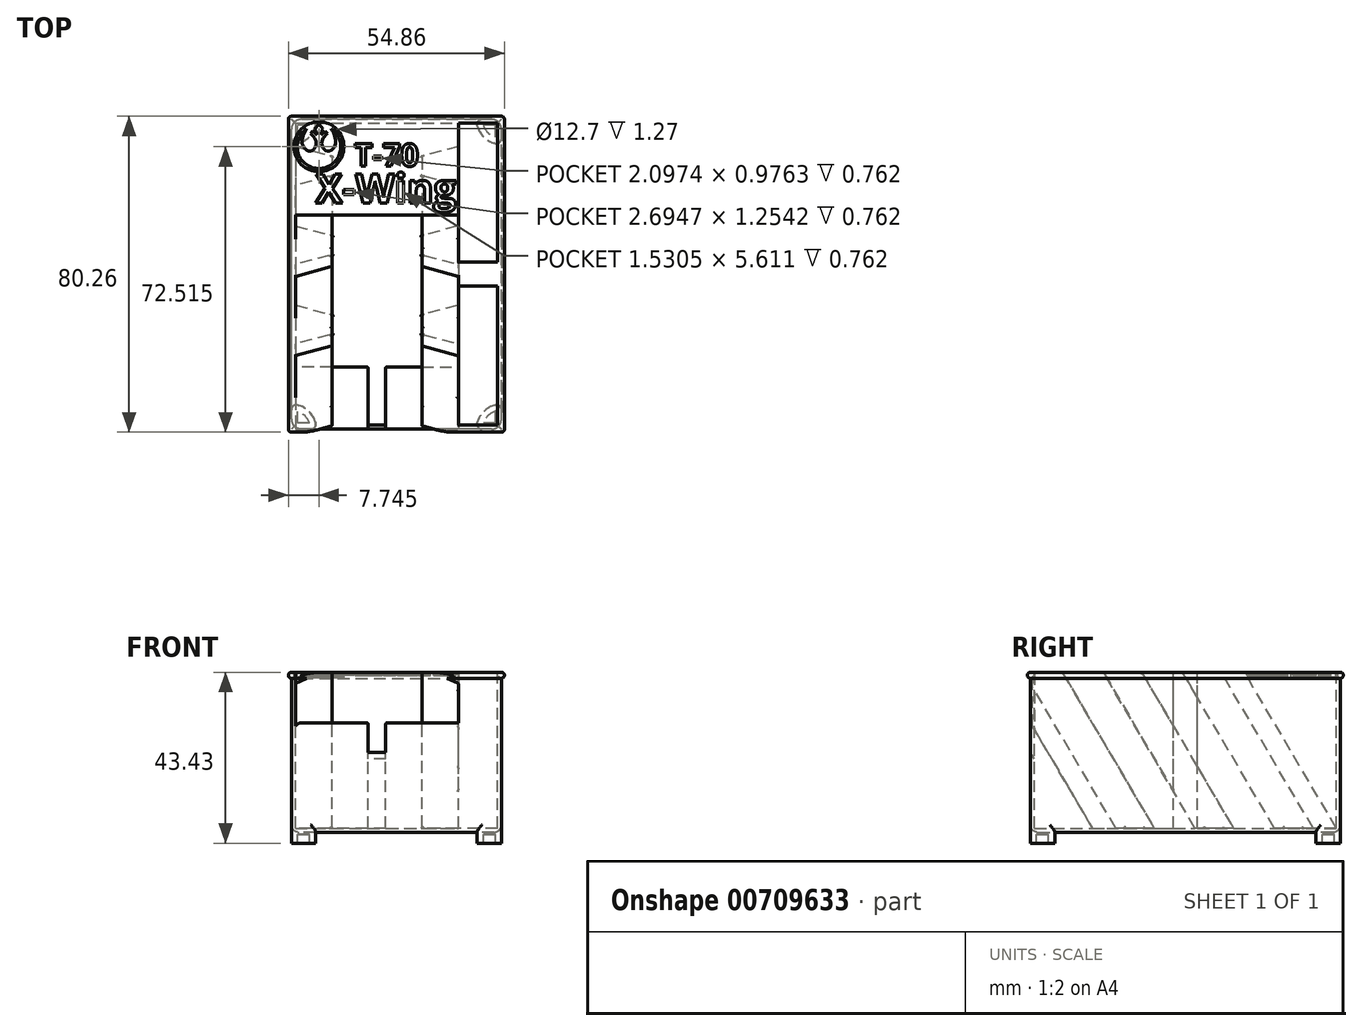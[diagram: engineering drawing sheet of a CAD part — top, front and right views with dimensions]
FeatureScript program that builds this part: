
annotation { "Feature Type Name" : "Feature", "Feature Type Description" : "" }
export const myFeature = defineFeature(function(context is Context, id is Id, definition is map)
    precondition{}
    {
        {
            var Q0;
            Q0=qCreatedBy(makeId("Top.planeOp"),FACE);
            var sketch = newSketch(context, id + "F0", { "sketchPlane" : qUnion([Q0])});
            skLineSegment(sketch, "E0.bottom", {"start": v(25.15, 37.85) * mm, "end": v(-25.15, 37.85) * mm});
            skLineSegment(sketch, "E0.top", {"start": v(25.15, -37.85) * mm, "end": v(-25.15, -37.85) * mm});
            skLineSegment(sketch, "E0.left", {"start": v(25.15, 37.85) * mm, "end": v(25.15, -37.85) * mm});
            skLineSegment(sketch, "E0.right", {"start": v(-25.15, 37.85) * mm, "end": v(-25.15, -37.85) * mm});
            skPoint(sketch, "E0.middle", {"position": v(0, 0) * mm});
            skSolve(sketch);
        }
        {
            var Q0;
            Q0=qCreatedBy(makeId("Front.planeOp"),FACE);
            var sketch = newSketch(context, id + "F1", { "sketchPlane" : qUnion([Q0])});
            skLineSegment(sketch, "E1.bottom", {"start": v(26.67, -20.32) * mm, "end": v(-26.67, -20.32) * mm});
            skLineSegment(sketch, "E1.top", {"start": v(26.67, 20.32) * mm, "end": v(-26.67, 20.32) * mm});
            skLineSegment(sketch, "E1.left", {"start": v(26.67, -20.32) * mm, "end": v(26.67, 20.32) * mm});
            skLineSegment(sketch, "E1.right", {"start": v(-26.67, -20.32) * mm, "end": v(-26.67, 20.32) * mm});
            skPoint(sketch, "E1.middle", {"position": v(0, 0) * mm});
            skSolve(sketch);
        }
        {
            var Q0;
            Q0=qSketchRegion(id+"F1",true);
            extrude(context, id + "F2", {"entities" : qUnion([Q0]), "depth" : 78.74 * mm, "offsetDistance" : 25.4 * mm, "symmetric" : true});
        }
        {
            var Q0;
            Q0=makeQuery(id+"F2.opExtrude","SWEPT_FACE",FACE,{"disambiguationData":[OSD([sQuery(id+"F1.wireOp",EDGE,"E1.top")])]});
            shell(context, id + "F3", {"entities" : qUnion([Q0]), "thickness" : 1.02 * mm});
        }
        {
            var Q0;
            {var subQ0=sQuery(id+"F1.wireOp",EDGE,"E1.right");var subQ3=sQuery(id+"F1.wireOp",EDGE,"E1.top");Q0=makeQuery(id+"F16.boolean.opBoolean","SPLIT",EDGE,{"disambiguationData":[TD([makeQuery(id+"F3.opShell","OFFSET_FACE",FACE,{"disambiguationData":[OSD([subQ0])]})])],"derivedFrom":makeQuery(id+"F3.opShell","OFFSET_EDGE",EDGE,{"disambiguationData":[OSD([subQ3]),TDD([makeQuery(id+"F2.opExtrude","CAP_EDGE",EDGE,{"disambiguationData":[OSD([subQ3])],"isStart":false})])]})});}
            var Q1;
            {var subQ0=sQuery(id+"F7.wireOp",EDGE,"E9");var subQ1=sQuery(id+"F1.wireOp",EDGE,"E1.right");var subQ2=sQuery(id+"F1.wireOp",EDGE,"E1.top");var subQ3=makeQuery(id+"F2.opExtrude","CAP_EDGE",EDGE,{"disambiguationData":[OSD([subQ2])],"isStart":false});Q1=makeQuery(id+"F8.boolean.opBoolean","MERGE",EDGE,{"derivedFrom":[subQ3,makeQuery(id+"F8.opSweep","SWEPT_EDGE",EDGE,{"disambiguationData":[OSD([subQ2,subQ1,subQ0]),TDD([subQ3,makeQuery(id+"F7.imprint","INTERSECT",VERTEX,{"derivedFrom":[subQ3,makeQuery(id+"F2.opExtrude","CAP_EDGE",EDGE,{"disambiguationData":[OSD([subQ1])],"isStart":false}),subQ0]})])]})]});}
            cPlane(context, id + "F4", {"entities" : qUnion([Q0, Q1]), "cplaneType" : CPlaneType.LINE_ANGLE, "offset" : 25.4 * mm, "angle" : 30.5 * degree, "oppositeDirection" : true, "width" : 152.4 * mm, "height" : 152.4 * mm});
        }
        {
            var Q0;
            Q0=makeQuery(id+"F3.opShell","OFFSET_FACE",FACE,{"disambiguationData":[OSD([sQuery(id+"F1.wireOp",EDGE,"E1.right")])]});
            var sketch = newSketch(context, id + "F5", { "sketchPlane" : qUnion([Q0])});
            skLineSegment(sketch, "E2.0", {"start": v(38.35, -19.3) * mm, "end": v(38.35, 20.32) * mm});
            skLineSegment(sketch, "E3.1", {"start": v(-38.35, -19.3) * mm, "end": v(38.35, -19.3) * mm});
            skLineSegment(sketch, "E4", {"start": v(38.35, -19.3) * mm, "end": v(-5.55, 55.23) * mm});
            skLineSegment(sketch, "E5.0", {"start": v(-38.35, 20.32) * mm, "end": v(38.35, 20.32) * mm});
            skPoint(sketch, "E6", {"position": v(15.01, 20.32) * mm});
            skSolve(sketch);
        }
        {
            var Q0;
            Q0=qCreatedBy(id+"F4.planeOp",FACE);
            var sketch = newSketch(context, id + "F6", { "sketchPlane" : qUnion([Q0])});
            skPoint(sketch, "E7.0", {"position": v(-25.65, 23.25) * mm});
            skSolve(sketch);
        }
        {
            var Q0;
            Q0=makeQuery(id+"F2.opExtrude","CAP_FACE",FACE,{"disambiguationData":[OSD([sQuery(id+"F1.wireOp",EDGE,"E1.bottom"),sQuery(id+"F1.wireOp",EDGE,"E1.top"),sQuery(id+"F1.wireOp",EDGE,"E1.left"),sQuery(id+"F1.wireOp",EDGE,"E1.right")])],"isStart":false});
            var sketch = newSketch(context, id + "F7", { "sketchPlane" : qUnion([Q0])});
            skArc(sketch, "E8", {"start": v(-122.9, 118.26) * mm, "mid": v(-123.67, 117.5) * mm, "end": v(-122.9, 116.74) * mm});
            skArc(sketch, "E9", {"start": v(-26.67, 20.32) * mm, "mid": v(-27.43, 19.56) * mm, "end": v(-26.67, 18.8) * mm});
            skSolve(sketch);
        }
        {
            var Q0;
            {var subQ0=sQuery(id+"F7.wireOp",EDGE,"E9");Q0=makeQuery(id+"F7.imprint","IMPRINT",FACE,{"disambiguationData":[TD([[makeQuery(id+"F7.imprint","IMPRINT",EDGE,{"derivedFrom":subQ0}),1.0]])]});}
            var Q1;
            Q1=makeQuery(id+"F2.opExtrude","CAP_EDGE",EDGE,{"disambiguationData":[OSD([sQuery(id+"F1.wireOp",EDGE,"E1.top")])],"isStart":false});
            var Q2;
            Q2=makeQuery(id+"F2.opExtrude","SWEPT_EDGE",EDGE,{"disambiguationData":[OSD([sQuery(id+"F1.wireOp",EDGE,"E1.top"),sQuery(id+"F1.wireOp",EDGE,"E1.right")])]});
            var Q3;
            Q3=makeQuery(id+"F2.opExtrude","SWEPT_EDGE",EDGE,{"disambiguationData":[OSD([sQuery(id+"F1.wireOp",EDGE,"E1.top"),sQuery(id+"F1.wireOp",EDGE,"E1.left")])]});
            var Q4;
            Q4=makeQuery(id+"F2.opExtrude","CAP_EDGE",EDGE,{"disambiguationData":[OSD([sQuery(id+"F1.wireOp",EDGE,"E1.top")])],"isStart":true});
            sweep(context, id + "F8", {"operationType" : NewBodyOperationType.ADD, "profiles" : qUnion([Q0]), "path" : qUnion([Q1, Q2, Q3, Q4])});
        }
        {
            var Q0;
            Q0=makeQuery(id+"F2.opExtrude","SWEPT_FACE",FACE,{"disambiguationData":[OSD([sQuery(id+"F1.wireOp",EDGE,"E1.bottom")])]});
            var sketch = newSketch(context, id + "F9", { "sketchPlane" : qUnion([Q0])});
            skLineSegment(sketch, "E10.bottom", {"start": v(26.67, 39.37) * mm, "end": v(21.75, 39.37) * mm});
            skLineSegment(sketch, "E10.left", {"start": v(26.67, 39.37) * mm, "end": v(26.67, 34.45) * mm});
            skPoint(sketch, "E11.newPointA", {"position": v(20.32, 19.05) * mm});
            skArc(sketch, "E12", {"start": v(20.52, 37.78) * mm, "mid": v(22.18, 34.88) * mm, "end": v(25.08, 33.22) * mm});
            skPoint(sketch, "E13.visualSharp", {"position": v(20.32, 39.37) * mm});
            skArc(sketch, "E13.filletArc", {"start": v(21.75, 39.37) * mm, "mid": v(20.75, 38.88) * mm, "end": v(20.52, 37.78) * mm});
            skPoint(sketch, "E14.visualSharp", {"position": v(26.67, 33.02) * mm});
            skArc(sketch, "E14.filletArc", {"start": v(25.08, 33.22) * mm, "mid": v(26.18, 33.45) * mm, "end": v(26.67, 34.45) * mm});
            skArc(sketch, "E15.MirrorCS", {"start": v(-21.75, 39.37) * mm, "mid": v(-20.75, 38.88) * mm, "end": v(-20.52, 37.78) * mm});
            skArc(sketch, "E16.MirrorCS", {"start": v(-20.52, 37.78) * mm, "mid": v(-22.18, 34.88) * mm, "end": v(-25.08, 33.22) * mm});
            skArc(sketch, "E17.MirrorCS", {"start": v(-25.08, 33.22) * mm, "mid": v(-26.18, 33.45) * mm, "end": v(-26.67, 34.45) * mm});
            skLineSegment(sketch, "E18.MirrorCS", {"start": v(-26.67, 39.37) * mm, "end": v(-26.67, 34.45) * mm});
            skLineSegment(sketch, "E19.MirrorCS", {"start": v(-26.67, 39.37) * mm, "end": v(-21.75, 39.37) * mm});
            skArc(sketch, "E20.MirrorCS", {"start": v(-20.52, -37.78) * mm, "mid": v(-22.18, -34.88) * mm, "end": v(-25.08, -33.22) * mm});
            skArc(sketch, "E21.MirrorCS", {"start": v(-21.75, -39.37) * mm, "mid": v(-20.75, -38.88) * mm, "end": v(-20.52, -37.78) * mm});
            skLineSegment(sketch, "E22.MirrorCS", {"start": v(-26.67, -39.37) * mm, "end": v(-21.75, -39.37) * mm});
            skLineSegment(sketch, "E23.MirrorCS", {"start": v(-26.67, -39.37) * mm, "end": v(-26.67, -34.45) * mm});
            skArc(sketch, "E24.MirrorCS", {"start": v(-25.08, -33.22) * mm, "mid": v(-26.18, -33.45) * mm, "end": v(-26.67, -34.45) * mm});
            skArc(sketch, "E25.MirrorCS", {"start": v(21.75, -39.37) * mm, "mid": v(20.75, -38.88) * mm, "end": v(20.52, -37.78) * mm});
            skArc(sketch, "E26.MirrorCS", {"start": v(20.52, -37.78) * mm, "mid": v(22.18, -34.88) * mm, "end": v(25.08, -33.22) * mm});
            skArc(sketch, "E27.MirrorCS", {"start": v(25.08, -33.22) * mm, "mid": v(26.18, -33.45) * mm, "end": v(26.67, -34.45) * mm});
            skLineSegment(sketch, "E28.MirrorCS", {"start": v(26.67, -39.37) * mm, "end": v(26.67, -34.45) * mm});
            skLineSegment(sketch, "E29.MirrorCS", {"start": v(26.67, -39.37) * mm, "end": v(21.75, -39.37) * mm});
            skSolve(sketch);
        }
        {
            var Q0;
            Q0=qSketchRegion(id+"F9",true);
            extrude(context, id + "F10", {"entities" : qUnion([Q0]), "operationType" : NewBodyOperationType.ADD, "depth" : 2.8 * mm, "offsetDistance" : 25.4 * mm});
        }
        {
            var Q0;
            Q0=makeQuery(id+"F10.opExtrude","CAP_FACE",FACE,{"disambiguationData":[OSD([sQuery(id+"F9.wireOp",EDGE,"E16.MirrorCS"),sQuery(id+"F9.wireOp",EDGE,"E17.MirrorCS"),sQuery(id+"F9.wireOp",EDGE,"E18.MirrorCS"),sQuery(id+"F9.wireOp",EDGE,"E15.MirrorCS"),sQuery(id+"F9.wireOp",EDGE,"E19.MirrorCS")])],"isStart":false});
            var Q1;
            Q1=makeQuery(id+"F10.opExtrude","CAP_FACE",FACE,{"disambiguationData":[OSD([sQuery(id+"F9.wireOp",EDGE,"E10.bottom"),sQuery(id+"F9.wireOp",EDGE,"E10.left"),sQuery(id+"F9.wireOp",EDGE,"E12"),sQuery(id+"F9.wireOp",EDGE,"E13.filletArc"),sQuery(id+"F9.wireOp",EDGE,"E14.filletArc")])],"isStart":false});
            var Q2;
            Q2=makeQuery(id+"F10.opExtrude","CAP_FACE",FACE,{"disambiguationData":[OSD([sQuery(id+"F9.wireOp",EDGE,"E25.MirrorCS"),sQuery(id+"F9.wireOp",EDGE,"E26.MirrorCS"),sQuery(id+"F9.wireOp",EDGE,"E27.MirrorCS"),sQuery(id+"F9.wireOp",EDGE,"E28.MirrorCS"),sQuery(id+"F9.wireOp",EDGE,"E29.MirrorCS")])],"isStart":false});
            var Q3;
            Q3=makeQuery(id+"F10.opExtrude","CAP_FACE",FACE,{"disambiguationData":[OSD([sQuery(id+"F9.wireOp",EDGE,"E20.MirrorCS"),sQuery(id+"F9.wireOp",EDGE,"E21.MirrorCS"),sQuery(id+"F9.wireOp",EDGE,"E22.MirrorCS"),sQuery(id+"F9.wireOp",EDGE,"E23.MirrorCS"),sQuery(id+"F9.wireOp",EDGE,"E24.MirrorCS")])],"isStart":false});
            shell(context, id + "F11", {"entities" : qUnion([Q0, Q1, Q2, Q3]), "thickness" : 1.52 * mm});
        }
        {
            var Q0;
            Q0=makeQuery(id+"F8.opSweep","MID_CAP_EDGE",EDGE,{"disambiguationData":[OSD([sQuery(id+"F1.wireOp",EDGE,"E1.top"),sQuery(id+"F1.wireOp",EDGE,"E1.right"),sQuery(id+"F7.wireOp",EDGE,"E9")])],"capPos":1.0});
            var Q1;
            Q1=makeQuery(id+"F8.opSweep","CAP_EDGE",EDGE,{"disambiguationData":[OSD([sQuery(id+"F1.wireOp",EDGE,"E1.top"),sQuery(id+"F1.wireOp",EDGE,"E1.right"),sQuery(id+"F7.wireOp",EDGE,"E9")])],"isStart":true});
            var Q2;
            Q2=makeQuery(id+"F8.opSweep","MID_CAP_EDGE",EDGE,{"disambiguationData":[OSD([sQuery(id+"F1.wireOp",EDGE,"E1.top"),sQuery(id+"F1.wireOp",EDGE,"E1.left"),sQuery(id+"F7.wireOp",EDGE,"E9")])],"capPos":3.0});
            var Q3;
            Q3=makeQuery(id+"F8.opSweep","MID_CAP_EDGE",EDGE,{"disambiguationData":[OSD([sQuery(id+"F1.wireOp",EDGE,"E1.top"),sQuery(id+"F1.wireOp",EDGE,"E1.left"),sQuery(id+"F7.wireOp",EDGE,"E9")])],"capPos":2.0});
            fillet(context, id + "F12", {"entities" : qUnion([Q0, Q1, Q2, Q3]), "radius" : 0.76 * mm, "tangentPropagation" : true, "allowEdgeOverflow" : false});
        }
        {
            var Q0;
            Q0=makeQuery(id+"F10.boolean.opBoolean","MERGE",EDGE,{"derivedFrom":[makeQuery(id+"F2.opExtrude","CAP_EDGE",EDGE,{"disambiguationData":[OSD([sQuery(id+"F1.wireOp",EDGE,"E1.right")])],"isStart":false}),makeQuery(id+"F10.opExtrude","SWEPT_EDGE",EDGE,{"disambiguationData":[OSD([sQuery(id+"F9.wireOp",EDGE,"E18.MirrorCS"),sQuery(id+"F9.wireOp",EDGE,"E19.MirrorCS")])]})]});
            var Q1;
            Q1=makeQuery(id+"F10.boolean.opBoolean","MERGE",EDGE,{"derivedFrom":[makeQuery(id+"F2.opExtrude","CAP_EDGE",EDGE,{"disambiguationData":[OSD([sQuery(id+"F1.wireOp",EDGE,"E1.left")])],"isStart":false}),makeQuery(id+"F10.opExtrude","SWEPT_EDGE",EDGE,{"disambiguationData":[OSD([sQuery(id+"F9.wireOp",EDGE,"E10.bottom"),sQuery(id+"F9.wireOp",EDGE,"E10.left")])]})]});
            var Q2;
            Q2=makeQuery(id+"F10.boolean.opBoolean","MERGE",EDGE,{"derivedFrom":[makeQuery(id+"F2.opExtrude","CAP_EDGE",EDGE,{"disambiguationData":[OSD([sQuery(id+"F1.wireOp",EDGE,"E1.left")])],"isStart":true}),makeQuery(id+"F10.opExtrude","SWEPT_EDGE",EDGE,{"disambiguationData":[OSD([sQuery(id+"F9.wireOp",EDGE,"E28.MirrorCS"),sQuery(id+"F9.wireOp",EDGE,"E29.MirrorCS")])]})]});
            var Q3;
            Q3=makeQuery(id+"F10.boolean.opBoolean","MERGE",EDGE,{"derivedFrom":[makeQuery(id+"F2.opExtrude","CAP_EDGE",EDGE,{"disambiguationData":[OSD([sQuery(id+"F1.wireOp",EDGE,"E1.right")])],"isStart":true}),makeQuery(id+"F10.opExtrude","SWEPT_EDGE",EDGE,{"disambiguationData":[OSD([sQuery(id+"F9.wireOp",EDGE,"E22.MirrorCS"),sQuery(id+"F9.wireOp",EDGE,"E23.MirrorCS")])]})]});
            fillet(context, id + "F13", {"entities" : qUnion([Q0, Q1, Q2, Q3]), "radius" : 2.54 * mm, "tangentPropagation" : true, "allowEdgeOverflow" : false});
        }
        {
            var Q0;
            Q0=makeQuery(id+"F2.opExtrude","SWEPT_EDGE",EDGE,{"disambiguationData":[OSD([sQuery(id+"F1.wireOp",EDGE,"E1.bottom"),sQuery(id+"F1.wireOp",EDGE,"E1.right")])]});
            var Q1;
            Q1=makeQuery(id+"F2.opExtrude","CAP_EDGE",EDGE,{"disambiguationData":[OSD([sQuery(id+"F1.wireOp",EDGE,"E1.bottom")])],"isStart":false});
            var Q2;
            Q2=makeQuery(id+"F2.opExtrude","SWEPT_EDGE",EDGE,{"disambiguationData":[OSD([sQuery(id+"F1.wireOp",EDGE,"E1.bottom"),sQuery(id+"F1.wireOp",EDGE,"E1.left")])]});
            var Q3;
            Q3=makeQuery(id+"F2.opExtrude","CAP_EDGE",EDGE,{"disambiguationData":[OSD([sQuery(id+"F1.wireOp",EDGE,"E1.bottom")])],"isStart":true});
            fillet(context, id + "F14", {"entities" : qUnion([Q0, Q1, Q2, Q3]), "radius" : 1.9 * mm, "tangentPropagation" : true, "allowEdgeOverflow" : false});
        }
        {
            var Q0;
            Q0=makeQuery(id+"F24.boolean.opBoolean","MERGE",FACE,{"derivedFrom":[makeQuery(id+"F2.opExtrude","SWEPT_FACE",FACE,{"disambiguationData":[OSD([sQuery(id+"F1.wireOp",EDGE,"E1.top")])]}),makeQuery(id+"F24.opExtrude","CAP_FACE",FACE,{"disambiguationData":[OSD([sQuery(id+"F23.wireOp",EDGE,"CeT5EqMD-vzeh-J7pB-LkoM-5uFaC58c3kCY.bottom"),sQuery(id+"F23.wireOp",EDGE,"CeT5EqMD-vzeh-J7pB-LkoM-5uFaC58c3kCY.top"),sQuery(id+"F23.wireOp",EDGE,"CeT5EqMD-vzeh-J7pB-LkoM-5uFaC58c3kCY.left"),sQuery(id+"F23.wireOp",EDGE,"CeT5EqMD-vzeh-J7pB-LkoM-5uFaC58c3kCY.right")])],"isStart":true})]});
            var sketch = newSketch(context, id + "F15", { "sketchPlane" : qUnion([Q0])});
            skLineSegment(sketch, "E30.bottom", {"start": v(25.65, 38.35) * mm, "end": v(15.75, 38.35) * mm});
            skLineSegment(sketch, "E30.top", {"start": v(25.65, 3.05) * mm, "end": v(15.75, 3.05) * mm});
            skLineSegment(sketch, "E30.left", {"start": v(25.65, 38.35) * mm, "end": v(25.65, 3.05) * mm});
            skLineSegment(sketch, "E30.right", {"start": v(15.75, 38.35) * mm, "end": v(15.75, 3.05) * mm});
            skLineSegment(sketch, "E31.bottom", {"start": v(25.65, -38.35) * mm, "end": v(15.75, -38.35) * mm});
            skLineSegment(sketch, "E31.top", {"start": v(25.65, -3.05) * mm, "end": v(15.75, -3.05) * mm});
            skLineSegment(sketch, "E31.left", {"start": v(25.65, -38.35) * mm, "end": v(25.65, -3.05) * mm});
            skLineSegment(sketch, "E31.right", {"start": v(15.75, -38.35) * mm, "end": v(15.75, -3.05) * mm});
            skLineSegment(sketch, "E32.bottom", {"start": v(25.65, 38.35) * mm, "end": v(-25.65, 38.35) * mm});
            skLineSegment(sketch, "E32.top", {"start": v(25.65, -38.35) * mm, "end": v(-25.65, -38.35) * mm});
            skLineSegment(sketch, "E32.left", {"start": v(25.65, 38.35) * mm, "end": v(25.65, -38.35) * mm});
            skLineSegment(sketch, "E32.right", {"start": v(-25.65, 38.35) * mm, "end": v(-25.65, -38.35) * mm});
            skLineSegment(sketch, "E33", {"start": v(15.75, -38.35) * mm, "end": v(15.75, -38.35) * mm});
            skLineSegment(sketch, "E34", {"start": v(15.75, -38.35) * mm, "end": v(15.75, 38.35) * mm});
            skLineSegment(sketch, "E35.0", {"start": v(-25.65, 38.35) * mm, "end": v(-25.65, -5.55) * mm});
            skPoint(sketch, "E36.0", {"position": v(-25.65, 15.01) * mm});
            skLineSegment(sketch, "E37", {"start": v(-25.65, 15.01) * mm, "end": v(15.75, 15.01) * mm});
            skSolve(sketch);
        }
        {
            var Q0;
            {var subQ3=sQuery(id+"F15.wireOp",EDGE,"E30.top");Q0=makeQuery(id+"F15.imprint","IMPRINT",FACE,{"disambiguationData":[TD([[makeQuery(id+"F15.imprint","IMPRINT",EDGE,{"derivedFrom":subQ3}),1.0]])]});}
            var Q1;
            {var subQ5=sQuery(id+"F15.wireOp",EDGE,"E37");Q1=makeQuery(id+"F15.imprint","IMPRINT",FACE,{"disambiguationData":[TD([[makeQuery(id+"F15.imprint","IMPRINT",EDGE,{"derivedFrom":subQ5}),1.0]])]});}
            var Q2;
            Q2=makeQuery(id+"F3.opShell","OFFSET_FACE",FACE,{"disambiguationData":[OSD([sQuery(id+"F1.wireOp",EDGE,"E1.bottom")])]});
            extrude(context, id + "F16", {"entities" : qUnion([Q0, Q1]), "operationType" : NewBodyOperationType.ADD, "endBound" : BoundingType.UP_TO_SURFACE, "oppositeDirection" : true, "depth" : 25.4 * mm, "endBoundEntityFace" : qUnion([Q2]), "offsetDistance" : 25.4 * mm});
        }
        {
            var Q0;
            Q0=qCreatedBy(id+"F4.planeOp",FACE);
            var sketch = newSketch(context, id + "F17", { "sketchPlane" : qUnion([Q0])});
            skLineSegment(sketch, "E38.0", {"start": v(-25.65, -16.56) * mm, "end": v(-25.65, -7.67) * mm});
            skLineSegment(sketch, "E39", {"start": v(-25.65, 23.25) * mm, "end": v(-4.95, 23.25) * mm});
            skPoint(sketch, "E40.0", {"position": v(-25.65, 23.25) * mm});
            skLineSegment(sketch, "E41", {"start": v(-25.65, 23.25) * mm, "end": v(-25.65, 18.17) * mm});
            skLineSegment(sketch, "E42", {"start": v(-25.65, 18.17) * mm, "end": v(-16.37, 16.03) * mm});
            skLineSegment(sketch, "E43", {"start": v(-16.37, 16.03) * mm, "end": v(-16.37, 11.84) * mm});
            skLineSegment(sketch, "E44", {"start": v(-16.37, 11.84) * mm, "end": v(-25.65, 9.7) * mm});
            skLineSegment(sketch, "E45", {"start": v(-25.65, 9.7) * mm, "end": v(-25.65, 0.8) * mm});
            skLineSegment(sketch, "E46", {"start": v(-25.65, 0.8) * mm, "end": v(-16.37, -1.34) * mm});
            skLineSegment(sketch, "E47", {"start": v(-16.37, -1.34) * mm, "end": v(-16.37, -5.53) * mm});
            skLineSegment(sketch, "E48", {"start": v(-16.37, -5.53) * mm, "end": v(-25.65, -7.67) * mm});
            skLineSegment(sketch, "E49", {"start": v(-25.65, -7.67) * mm, "end": v(-25.65, -16.56) * mm});
            skLineSegment(sketch, "E50", {"start": v(-25.65, -16.56) * mm, "end": v(-16.37, -18.7) * mm});
            skLineSegment(sketch, "E51", {"start": v(-16.37, -18.7) * mm, "end": v(-16.37, -22.9) * mm});
            skLineSegment(sketch, "E52", {"start": v(-16.37, -22.9) * mm, "end": v(-25.65, -25.04) * mm});
            skLineSegment(sketch, "E53", {"start": v(-25.65, -25.04) * mm, "end": v(-25.65, -30.12) * mm});
            skLineSegment(sketch, "E54", {"start": v(-25.65, -30.12) * mm, "end": v(-7.18, -30.12) * mm});
            skLineSegment(sketch, "E55", {"start": v(-7.18, -30.12) * mm, "end": v(-7.18, -33.93) * mm});
            skLineSegment(sketch, "E56", {"start": v(-7.18, -33.93) * mm, "end": v(-4.95, -33.93) * mm});
            skLineSegment(sketch, "E57.trimOffspring", {"start": v(-25.65, 0.8) * mm, "end": v(-25.65, 9.7) * mm});
            skLineSegment(sketch, "E58.trimOffspring", {"start": v(-25.65, 18.17) * mm, "end": v(-25.65, 23.25) * mm});
            skPoint(sketch, "E59.orphan", {"position": v(-25.65, -22.73) * mm});
            skLineSegment(sketch, "E60", {"start": v(-4.95, -94.16) * mm, "end": v(-4.95, 57.75) * mm});
            skLineSegment(sketch, "E61.MirrorCS", {"start": v(15.75, 23.25) * mm, "end": v(15.75, 18.17) * mm});
            skLineSegment(sketch, "E62.MirrorCS", {"start": v(6.47, -1.34) * mm, "end": v(6.47, -5.53) * mm});
            skLineSegment(sketch, "E63.MirrorCS", {"start": v(-2.73, -33.93) * mm, "end": v(-4.95, -33.93) * mm});
            skLineSegment(sketch, "E64.MirrorCS", {"start": v(15.75, 18.17) * mm, "end": v(15.75, 23.25) * mm});
            skLineSegment(sketch, "E65.MirrorCS", {"start": v(6.47, 16.03) * mm, "end": v(6.47, 11.84) * mm});
            skLineSegment(sketch, "E66.MirrorCS", {"start": v(6.47, -18.7) * mm, "end": v(6.47, -22.9) * mm});
            skLineSegment(sketch, "E67.MirrorCS", {"start": v(15.75, -16.56) * mm, "end": v(15.75, -7.67) * mm});
            skLineSegment(sketch, "E68.MirrorCS", {"start": v(-2.73, -30.12) * mm, "end": v(-2.73, -33.93) * mm});
            skLineSegment(sketch, "E69.MirrorCS", {"start": v(15.75, 18.17) * mm, "end": v(6.47, 16.03) * mm});
            skLineSegment(sketch, "E70.MirrorCS", {"start": v(6.47, 11.84) * mm, "end": v(15.75, 9.7) * mm});
            skLineSegment(sketch, "E71.MirrorCS", {"start": v(15.75, 0.8) * mm, "end": v(15.75, 9.7) * mm});
            skLineSegment(sketch, "E72.MirrorCS", {"start": v(15.75, -7.67) * mm, "end": v(15.75, -16.56) * mm});
            skLineSegment(sketch, "E73.MirrorCS", {"start": v(6.47, -5.53) * mm, "end": v(15.75, -7.67) * mm});
            skLineSegment(sketch, "E74.MirrorCS", {"start": v(6.47, -22.9) * mm, "end": v(15.75, -25.04) * mm});
            skPoint(sketch, "E75.MirrorP", {"position": v(15.75, -22.73) * mm});
            skLineSegment(sketch, "E76.MirrorCS", {"start": v(15.75, -16.56) * mm, "end": v(6.47, -18.7) * mm});
            skLineSegment(sketch, "E77.MirrorCS", {"start": v(15.75, -25.04) * mm, "end": v(15.75, -30.12) * mm});
            skLineSegment(sketch, "E78.MirrorCS", {"start": v(15.75, -30.12) * mm, "end": v(-2.73, -30.12) * mm});
            skLineSegment(sketch, "E79.MirrorCS", {"start": v(15.75, 0.8) * mm, "end": v(6.47, -1.34) * mm});
            skLineSegment(sketch, "E80.MirrorCS", {"start": v(15.75, 23.25) * mm, "end": v(-4.95, 23.25) * mm});
            skLineSegment(sketch, "E81.MirrorCS", {"start": v(15.75, 9.7) * mm, "end": v(15.75, 0.8) * mm});
            skPoint(sketch, "E82.MirrorP", {"position": v(15.75, 23.25) * mm});
            skLineSegment(sketch, "E83.bottom", {"start": v(-25.65, 23.25) * mm, "end": v(15.75, 23.25) * mm});
            skLineSegment(sketch, "E83.top", {"start": v(-25.65, -30.12) * mm, "end": v(15.75, -30.12) * mm});
            skLineSegment(sketch, "E83.left", {"start": v(-25.65, 23.25) * mm, "end": v(-25.65, -30.12) * mm});
            skLineSegment(sketch, "E83.right", {"start": v(15.75, 23.25) * mm, "end": v(15.75, -30.12) * mm});
            skSolve(sketch);
        }
        {
            var Q0;
            {var subQ0=sQuery(id+"F17.wireOp",EDGE,"E42");Q0=makeQuery(id+"F17.imprint","IMPRINT",FACE,{"disambiguationData":[TD([[makeQuery(id+"F17.imprint","IMPRINT",EDGE,{"derivedFrom":subQ0}),-1.0]])]});}
            var Q1;
            {var subQ0=sQuery(id+"F17.wireOp",EDGE,"E46");Q1=makeQuery(id+"F17.imprint","IMPRINT",FACE,{"disambiguationData":[TD([[makeQuery(id+"F17.imprint","IMPRINT",EDGE,{"derivedFrom":subQ0}),-1.0]])]});}
            var Q2;
            {var subQ0=sQuery(id+"F17.wireOp",EDGE,"E50");Q2=makeQuery(id+"F17.imprint","IMPRINT",FACE,{"disambiguationData":[TD([[makeQuery(id+"F17.imprint","IMPRINT",EDGE,{"derivedFrom":subQ0}),-1.0]])]});}
            var Q3;
            Q3=makeQuery(id+"F17.imprint","IMPRINT",FACE,{"disambiguationData":[TD([[makeQuery(id+"F17.imprint","IMPRINT",EDGE,{"derivedFrom":sQuery(id+"F17.wireOp",EDGE,"E66.MirrorCS")}),1.0]])]});
            var Q4;
            Q4=makeQuery(id+"F17.imprint","IMPRINT",FACE,{"disambiguationData":[TD([[makeQuery(id+"F17.imprint","IMPRINT",EDGE,{"derivedFrom":sQuery(id+"F17.wireOp",EDGE,"E62.MirrorCS")}),1.0]])]});
            var Q5;
            Q5=makeQuery(id+"F17.imprint","IMPRINT",FACE,{"disambiguationData":[TD([[makeQuery(id+"F17.imprint","IMPRINT",EDGE,{"derivedFrom":sQuery(id+"F17.wireOp",EDGE,"E65.MirrorCS")}),1.0]])]});
            extrude(context, id + "F18", {"entities" : qUnion([Q0, Q1, Q2, Q3, Q4, Q5]), "operationType" : NewBodyOperationType.ADD, "endBound" : BoundingType.UP_TO_NEXT, "oppositeDirection" : true, "depth" : 25.4 * mm, "offsetDistance" : 25.4 * mm});
        }
        {
            var Q0;
            {var subQ2=sQuery(id+"F17.wireOp",EDGE,"E42");Q0=makeQuery(id+"F17.imprint","IMPRINT",FACE,{"disambiguationData":[TD([[makeQuery(id+"F17.imprint","IMPRINT",EDGE,{"derivedFrom":subQ2}),1.0]])]});}
            var Q1;
            Q1=makeQuery(id+"F17.imprint","IMPRINT",FACE,{"disambiguationData":[TD([[makeQuery(id+"F17.imprint","IMPRINT",EDGE,{"derivedFrom":sQuery(id+"F17.wireOp",EDGE,"E62.MirrorCS")}),-1.0]])]});
            var Q2;
            {var subQ0=sQuery(id+"F17.wireOp",EDGE,"E63.MirrorCS");Q2=makeQuery(id+"F17.imprint","IMPRINT",FACE,{"disambiguationData":[TD([[makeQuery(id+"F17.imprint","IMPRINT",EDGE,{"derivedFrom":subQ0}),-1.0]])]});}
            var Q3;
            {var subQ0=sQuery(id+"F17.wireOp",EDGE,"E55");Q3=makeQuery(id+"F17.imprint","IMPRINT",FACE,{"disambiguationData":[TD([[makeQuery(id+"F17.imprint","IMPRINT",EDGE,{"derivedFrom":subQ0}),1.0]])]});}
            var Q4;
            {var subQ0=sQuery(id+"F1.wireOp",EDGE,"E1.right");var subQ3=sQuery(id+"F1.wireOp",EDGE,"E1.bottom");Q4=makeQuery(id+"F16.boolean.opBoolean","SPLIT",FACE,{"disambiguationData":[TD([makeQuery(id+"F3.opShell","OFFSET_FACE",FACE,{"disambiguationData":[OSD([subQ0])]})])],"derivedFrom":makeQuery(id+"F3.opShell","OFFSET_FACE",FACE,{"disambiguationData":[OSD([subQ3])]})});}
            extrude(context, id + "F19", {"entities" : qUnion([Q0, Q1, Q2, Q3]), "operationType" : NewBodyOperationType.REMOVE, "endBound" : BoundingType.UP_TO_SURFACE, "oppositeDirection" : true, "depth" : 25.4 * mm, "endBoundEntityFace" : qUnion([Q4]), "offsetDistance" : 25.4 * mm});
        }
        {
            var Q0;
            {var subQ2=sQuery(id+"F17.wireOp",EDGE,"E42");Q0=makeQuery(id+"F17.imprint","IMPRINT",FACE,{"disambiguationData":[TD([[makeQuery(id+"F17.imprint","IMPRINT",EDGE,{"derivedFrom":subQ2}),1.0]])]});}
            var Q1;
            Q1=makeQuery(id+"F17.imprint","IMPRINT",FACE,{"disambiguationData":[TD([[makeQuery(id+"F17.imprint","IMPRINT",EDGE,{"derivedFrom":sQuery(id+"F17.wireOp",EDGE,"E62.MirrorCS")}),-1.0]])]});
            var Q2;
            {var subQ0=sQuery(id+"F17.wireOp",EDGE,"E63.MirrorCS");Q2=makeQuery(id+"F17.imprint","IMPRINT",FACE,{"disambiguationData":[TD([[makeQuery(id+"F17.imprint","IMPRINT",EDGE,{"derivedFrom":subQ0}),-1.0]])]});}
            var Q3;
            {var subQ0=sQuery(id+"F17.wireOp",EDGE,"E55");Q3=makeQuery(id+"F17.imprint","IMPRINT",FACE,{"disambiguationData":[TD([[makeQuery(id+"F17.imprint","IMPRINT",EDGE,{"derivedFrom":subQ0}),1.0]])]});}
            extrude(context, id + "F20", {"entities" : qUnion([Q0, Q1, Q2, Q3]), "operationType" : NewBodyOperationType.REMOVE, "depth" : 25.4 * mm, "offsetDistance" : 25.4 * mm});
        }
        {
            var Q0;
            Q0=makeQuery(id+"F16.boolean.opBoolean","MERGE",FACE,{"derivedFrom":[makeQuery(id+"F2.opExtrude","SWEPT_FACE",FACE,{"disambiguationData":[OSD([sQuery(id+"F1.wireOp",EDGE,"E1.top")])]}),makeQuery(id+"F16.opExtrude","CAP_FACE",FACE,{"disambiguationData":[OSD([sQuery(id+"F15.wireOp",EDGE,"hc8ozTBv-Tm9a-kJ22-CKKE-tXYxZ9j7C9O8.right"),sQuery(id+"F15.wireOp",EDGE,"axl2OUU4-iXIp-PN5l-KddX-B3juGezwyh9M"),sQuery(id+"F15.wireOp",EDGE,"pRjz3Pr6-j7dV-o5ry-EZdA-GTtMzoIt95sS"),sQuery(id+"F15.wireOp",EDGE,"v856Wygs-yZXH-i2VT-3ghV-dVD4C32cBXVV"),sQuery(id+"F15.wireOp",EDGE,"USvI0tPl-EBY3-tKBE-jOEe-J8Xq5xi1xeiV"),sQuery(id+"F15.wireOp",EDGE,"k8kRmxcm-2nWE-OpHm-94qM-GIo2QhKUa4bU"),sQuery(id+"F15.wireOp",EDGE,"X1O9FMfb-903Z-7eNO-K9uC-zuuZ2nm40ufy"),sQuery(id+"F15.wireOp",EDGE,"r2gNmgJv-KwMP-WI78-23uA-wNcYgOeBLYQq"),sQuery(id+"F15.wireOp",EDGE,"vQvzNP03-p6BG-Xv0D-D307-GviAW00GZ98y"),sQuery(id+"F15.wireOp",EDGE,"9BoKh5av-tXag-cxfd-tblm-Vw8L67vS9qZj")])],"isStart":true})]});
            var sketch = newSketch(context, id + "F21", { "sketchPlane" : qUnion([Q0])});
            skPoint(sketch, "E84.0", {"position": v(-26.67, 39.37) * mm});
            skPoint(sketch, "E85.0", {"position": v(26.67, -39.37) * mm});
            skLineSegment(sketch, "E86.bottom", {"start": v(-26.67, 39.37) * mm, "end": v(26.67, 39.37) * mm});
            skLineSegment(sketch, "E86.top", {"start": v(-26.67, -39.37) * mm, "end": v(26.67, -39.37) * mm});
            skLineSegment(sketch, "E86.left", {"start": v(-26.67, 39.37) * mm, "end": v(-26.67, -39.37) * mm});
            skLineSegment(sketch, "E86.right", {"start": v(26.67, 39.37) * mm, "end": v(26.67, -39.37) * mm});
            skSolve(sketch);
        }
        {
            var Q0;
            Q0=qSketchRegion(id+"F21",true);
            extrude(context, id + "F22", {"entities" : qUnion([Q0]), "operationType" : NewBodyOperationType.REMOVE, "depth" : 76.2 * mm, "offsetDistance" : 25.4 * mm});
        }
        {
            var Q0;
            Q0=makeQuery(id+"F10.boolean.opBoolean","MERGE",FACE,{"derivedFrom":[makeQuery(id+"F2.opExtrude","SWEPT_FACE",FACE,{"disambiguationData":[OSD([sQuery(id+"F1.wireOp",EDGE,"E1.left")])]}),makeQuery(id+"F10.opExtrude","SWEPT_FACE",FACE,{"disambiguationData":[OSD([sQuery(id+"F9.wireOp",EDGE,"E10.left")])]}),makeQuery(id+"F10.opExtrude","SWEPT_FACE",FACE,{"disambiguationData":[OSD([sQuery(id+"F9.wireOp",EDGE,"E28.MirrorCS")])]})]});
            var sketch = newSketch(context, id + "F23", { "sketchPlane" : qUnion([Q0])});
            skLineSegment(sketch, "E87.0", {"start": v(-39.37, -23.11) * mm, "end": v(-39.37, 18.8) * mm});
            skArc(sketch, "E87.1", {"start": v(-39.37, 18.8) * mm, "mid": v(-40.13, 19.56) * mm, "end": v(-39.37, 20.32) * mm});
            skLineSegment(sketch, "E88", {"start": v(-39.37, 20.32) * mm, "end": v(-45.72, 20.32) * mm});
            skLineSegment(sketch, "E89", {"start": v(-45.72, 20.32) * mm, "end": v(-45.72, -23.11) * mm});
            skLineSegment(sketch, "E90", {"start": v(-45.72, -23.11) * mm, "end": v(-39.37, -23.11) * mm});
            skSolve(sketch);
        }
        {
            var Q0;
            Q0=qSketchRegion(id+"F23",true);
            extrude(context, id + "F24", {"entities" : qUnion([Q0]), "operationType" : NewBodyOperationType.REMOVE, "oppositeDirection" : true, "depth" : 152.4 * mm, "offsetDistance" : 25.4 * mm});
        }
        {
            var Q0;
            {var subQ2=sQuery(id+"F17.wireOp",EDGE,"E74.MirrorCS");var subQ5=sQuery(id+"F1.wireOp",EDGE,"E1.top");var subQ6=sQuery(id+"F17.wireOp",EDGE,"E83.right");Q0=makeQuery(id+"F18.boolean.opBoolean","SPLIT",FACE,{"disambiguationData":[TD([makeQuery(id+"F2.opExtrude","SWEPT_FACE",FACE,{"disambiguationData":[OSD([subQ5])]})])],"derivedFrom":makeQuery(id+"F18.opExtrude","SWEPT_FACE",FACE,{"disambiguationData":[OSD([subQ6]),TDD([makeQuery(id+"F17.imprint","IMPRINT",EDGE,{"disambiguationData":[TD([[makeQuery(id+"F17.imprint","INTERSECT",VERTEX,{"derivedFrom":[subQ2,subQ6]}),1.0]])],"derivedFrom":subQ6})])]})});}
            var sketch = newSketch(context, id + "F25", { "sketchPlane" : qUnion([Q0])});
            skLineSegment(sketch, "E91.0", {"start": v(-38.35, 5.77) * mm, "end": v(-39.37, 7.5) * mm});
            skLineSegment(sketch, "E92.0", {"start": v(-38.35, -19.3) * mm, "end": v(-38.35, 20.32) * mm});
            skLineSegment(sketch, "E93.0", {"start": v(-38.35, -19.3) * mm, "end": v(-3.05, -19.3) * mm});
            skLineSegment(sketch, "E94", {"start": v(-39.37, 7.5) * mm, "end": v(-21.26, -23.25) * mm});
            skSolve(sketch);
        }
        {
            var Q0;
            {var subQ0=sQuery(id+"F25.wireOp",EDGE,"E93.0");var subQ1=sQuery(id+"F25.wireOp",EDGE,"E92.0");var subQ2=makeQuery(id+"F25.imprint","INTERSECT",VERTEX,{"derivedFrom":[subQ1,subQ0]});Q0=makeQuery(id+"F25.imprint","IMPRINT",FACE,{"disambiguationData":[TD([[makeQuery(id+"F25.imprint","IMPRINT",EDGE,{"disambiguationData":[TD([[subQ2,-1.0]])],"derivedFrom":subQ1}),-1.0]])]});}
            var Q1;
            {var subQ0=sQuery(id+"F1.wireOp",EDGE,"E1.right");var subQ1=sQuery(id+"F1.wireOp",EDGE,"E1.left");var subQ2=sQuery(id+"F1.wireOp",EDGE,"E1.top");var subQ3=sQuery(id+"F1.wireOp",EDGE,"E1.bottom");Q1=makeQuery(id+"F19.boolean.opBoolean","INTERSECT",VERTEX,{"derivedFrom":[makeQuery(id+"F3.opShell","OFFSET_FACE",FACE,{"disambiguationData":[OSD([subQ3,subQ2,subQ1,subQ0]),TDD([makeQuery(id+"F2.opExtrude","CAP_FACE",FACE,{"disambiguationData":[OSD([subQ3,subQ2,subQ1,subQ0])],"isStart":false})])]}),makeQuery(id+"F19.opExtrude","SWEPT_FACE",FACE,{"disambiguationData":[OSD([sQuery(id+"F17.wireOp",EDGE,"E56"),sQuery(id+"F17.wireOp",EDGE,"E63.MirrorCS")])]}),makeQuery(id+"F19.opExtrude","SWEPT_FACE",FACE,{"disambiguationData":[OSD([sQuery(id+"F17.wireOp",EDGE,"E68.MirrorCS")])]})]});}
            extrude(context, id + "F26", {"entities" : qUnion([Q0]), "operationType" : NewBodyOperationType.ADD, "endBound" : BoundingType.UP_TO_VERTEX, "oppositeDirection" : true, "depth" : 25.4 * mm, "endBoundEntityVertex" : qUnion([Q1]), "offsetDistance" : 25.4 * mm});
        }
        {
            var Q0;
            {var subQ0=sQuery(id+"F17.wireOp",EDGE,"E83.left");var subQ1=sQuery(id+"F17.wireOp",EDGE,"E52");var subQ3=sQuery(id+"F1.wireOp",EDGE,"E1.right");Q0=makeQuery(id+"F19.boolean.opBoolean","MERGE",FACE,{"derivedFrom":[makeQuery(id+"F18.boolean.opBoolean","SPLIT",FACE,{"disambiguationData":[TD([makeQuery(id+"F18.opExtrude","SWEPT_FACE",FACE,{"disambiguationData":[OSD([subQ1])]})])],"derivedFrom":makeQuery(id+"F3.opShell","OFFSET_FACE",FACE,{"disambiguationData":[OSD([subQ3])]})}),makeQuery(id+"F19.opExtrude","SWEPT_FACE",FACE,{"disambiguationData":[OSD([subQ0]),TDD([makeQuery(id+"F17.imprint","IMPRINT",EDGE,{"disambiguationData":[TD([[makeQuery(id+"F17.imprint","INTERSECT",VERTEX,{"derivedFrom":[subQ1,subQ0]}),-1.0]])],"derivedFrom":subQ0})])]})]});}
            var sketch = newSketch(context, id + "F27", { "sketchPlane" : qUnion([Q0])});
            skLineSegment(sketch, "E95.0", {"start": v(-38.35, 5.77) * mm, "end": v(-38.86, 6.63) * mm});
            skLineSegment(sketch, "E96.0", {"start": v(-38.35, -19.3) * mm, "end": v(-38.35, 5.77) * mm});
            skLineSegment(sketch, "E97.0", {"start": v(-38.35, -19.3) * mm, "end": v(-17.69, -19.3) * mm});
            skLineSegment(sketch, "E98", {"start": v(-38.86, 6.63) * mm, "end": v(-21.34, -23.12) * mm});
            skSolve(sketch);
        }
        {
            var Q0;
            {var subQ0=sQuery(id+"F27.wireOp",EDGE,"E96.0");Q0=makeQuery(id+"F27.imprint","IMPRINT",FACE,{"disambiguationData":[TD([[makeQuery(id+"F27.imprint","IMPRINT",EDGE,{"derivedFrom":subQ0}),-1.0]])]});}
            var Q1;
            {var subQ0=sQuery(id+"F1.wireOp",EDGE,"E1.right");var subQ1=sQuery(id+"F1.wireOp",EDGE,"E1.left");var subQ2=sQuery(id+"F1.wireOp",EDGE,"E1.top");var subQ3=sQuery(id+"F1.wireOp",EDGE,"E1.bottom");Q1=makeQuery(id+"F19.boolean.opBoolean","INTERSECT",VERTEX,{"derivedFrom":[makeQuery(id+"F3.opShell","OFFSET_FACE",FACE,{"disambiguationData":[OSD([subQ3,subQ2,subQ1,subQ0]),TDD([makeQuery(id+"F2.opExtrude","CAP_FACE",FACE,{"disambiguationData":[OSD([subQ3,subQ2,subQ1,subQ0])],"isStart":false})])]}),makeQuery(id+"F19.opExtrude","SWEPT_FACE",FACE,{"disambiguationData":[OSD([sQuery(id+"F17.wireOp",EDGE,"E55")])]}),makeQuery(id+"F19.opExtrude","SWEPT_FACE",FACE,{"disambiguationData":[OSD([sQuery(id+"F17.wireOp",EDGE,"E56"),sQuery(id+"F17.wireOp",EDGE,"E63.MirrorCS")])]})]});}
            extrude(context, id + "F28", {"entities" : qUnion([Q0]), "operationType" : NewBodyOperationType.ADD, "endBound" : BoundingType.UP_TO_VERTEX, "depth" : 25.4 * mm, "endBoundEntityVertex" : qUnion([Q1]), "offsetDistance" : 25.4 * mm});
        }
        {
            var Q0;
            {var subQ0=sQuery(id+"F15.wireOp",EDGE,"E34");Q0=makeQuery(id+"F22.boolean.opBoolean","MERGE",FACE,{"derivedFrom":[makeQuery(id+"F16.boolean.opBoolean","MERGE",FACE,{"derivedFrom":[makeQuery(id+"F2.opExtrude","SWEPT_FACE",FACE,{"disambiguationData":[OSD([sQuery(id+"F1.wireOp",EDGE,"E1.top")])]}),makeQuery(id+"F16.opExtrude","CAP_FACE",FACE,{"disambiguationData":[OSD([sQuery(id+"F15.wireOp",EDGE,"E30.top"),sQuery(id+"F15.wireOp",EDGE,"E31.top"),sQuery(id+"F15.wireOp",EDGE,"E32.left"),subQ0])],"isStart":true}),makeQuery(id+"F16.opExtrude","CAP_FACE",FACE,{"disambiguationData":[OSD([sQuery(id+"F15.wireOp",EDGE,"E32.bottom"),subQ0,sQuery(id+"F15.wireOp",EDGE,"E35.0"),sQuery(id+"F15.wireOp",EDGE,"E37")])],"isStart":true})]}),makeQuery(id+"F22.opExtrude","CAP_FACE",FACE,{"disambiguationData":[OSD([sQuery(id+"F21.wireOp",EDGE,"E86.bottom"),sQuery(id+"F21.wireOp",EDGE,"E86.top"),sQuery(id+"F21.wireOp",EDGE,"E86.left"),sQuery(id+"F21.wireOp",EDGE,"E86.right")])],"isStart":true})]});}
            var sketch = newSketch(context, id + "F29", { "sketchPlane" : qUnion([Q0])});
            skCircle(sketch, "E99", {"center": v(-16.64, 70.48) * mm, "radius": 9.53 * mm});
            skArc(sketch, "E100", {"start": v(-16.64, 62.23) * mm, "mid": v(-8.77, 67.98) * mm, "end": v(-11.86, 77.22) * mm});
            skLineSegment(sketch, "E101", {"start": v(-16.64, 70.48) * mm, "end": v(-16.64, 78.74) * mm});
            skLineSegment(sketch, "E102", {"start": v(-16.64, 78.74) * mm, "end": v(-16.64, 62.23) * mm});
            skLineSegment(sketch, "E103", {"start": v(-16.64, 78.74) * mm, "end": v(-16.64, 79.22) * mm});
            skLineSegment(sketch, "E104", {"start": v(-15.04, 77.33) * mm, "end": v(-16.64, 79.22) * mm});
            skLineSegment(sketch, "E105", {"start": v(-14.3, 76.45) * mm, "end": v(-13.42, 75.41) * mm});
            skLineSegment(sketch, "E106", {"start": v(-13.42, 75.41) * mm, "end": v(-14.3, 76.45) * mm});
            skArc(sketch, "E107", {"start": v(-14.3, 76.45) * mm, "mid": v(-15.11, 75.72) * mm, "end": v(-15.82, 74.87) * mm});
            skArc(sketch, "E108", {"start": v(-15.04, 77.33) * mm, "mid": v(-15.62, 76.16) * mm, "end": v(-15.82, 74.87) * mm});
            skArc(sketch, "E109", {"start": v(-13.42, 75.41) * mm, "mid": v(-15.54, 72.08) * mm, "end": v(-13.42, 68.75) * mm});
            skArc(sketch, "E110", {"start": v(-14.05, 69.12) * mm, "mid": v(-12.27, 69.05) * mm, "end": v(-10.86, 70.15) * mm});
            skArc(sketch, "E111", {"start": v(-10.86, 70.15) * mm, "mid": v(-10.5, 73.8) * mm, "end": v(-11.86, 77.22) * mm});
            skLineSegment(sketch, "E112.MirrorCS", {"start": v(-18.98, 76.45) * mm, "end": v(-19.86, 75.41) * mm});
            skArc(sketch, "E113.MirrorCS", {"start": v(-18.23, 77.33) * mm, "mid": v(-17.65, 76.16) * mm, "end": v(-17.46, 74.87) * mm});
            skArc(sketch, "E114.MirrorCS", {"start": v(-19.86, 75.41) * mm, "mid": v(-17.73, 72.08) * mm, "end": v(-19.86, 68.75) * mm});
            skLineSegment(sketch, "E115.MirrorCS", {"start": v(-19.86, 75.41) * mm, "end": v(-18.98, 76.45) * mm});
            skLineSegment(sketch, "E116.MirrorCS", {"start": v(-18.23, 77.33) * mm, "end": v(-16.64, 79.22) * mm});
            skArc(sketch, "E117.MirrorCS", {"start": v(-16.64, 62.23) * mm, "mid": v(-24.5, 67.98) * mm, "end": v(-21.41, 77.22) * mm});
            skArc(sketch, "E118.MirrorCS", {"start": v(-18.98, 76.45) * mm, "mid": v(-18.16, 75.72) * mm, "end": v(-17.46, 74.87) * mm});
            skArc(sketch, "E119.MirrorCS", {"start": v(-22.41, 70.15) * mm, "mid": v(-22.77, 73.8) * mm, "end": v(-21.41, 77.22) * mm});
            skArc(sketch, "E120.MirrorCS", {"start": v(-19.23, 69.12) * mm, "mid": v(-21, 69.05) * mm, "end": v(-22.41, 70.15) * mm});
            skPoint(sketch, "E121.0", {"position": v(-26.16, 80) * mm});
            skLineSegment(sketch, "E122", {"start": v(-16.64, 80) * mm, "end": v(-16.64, 70.48) * mm});
            skCircle(sketch, "E123", {"center": v(22.86, 72.32) * mm, "radius": 7.9 * mm});
            skLineSegment(sketch, "E124", {"start": v(24.2, 78) * mm, "end": v(22.86, 79.54) * mm});
            skLineSegment(sketch, "E125", {"start": v(24.83, 77.3) * mm, "end": v(25.5, 76.42) * mm});
            skLineSegment(sketch, "E126", {"start": v(24.83, 77.3) * mm, "end": v(24.03, 76.6) * mm});
            skLineSegment(sketch, "E127", {"start": v(24.03, 76.6) * mm, "end": v(23.53, 75.98) * mm});
            skLineSegment(sketch, "E128", {"start": v(23.53, 75.98) * mm, "end": v(23.63, 76.79) * mm});
            skLineSegment(sketch, "E129", {"start": v(23.63, 76.79) * mm, "end": v(23.95, 77.61) * mm});
            skLineSegment(sketch, "E130", {"start": v(23.95, 77.61) * mm, "end": v(24.2, 78) * mm});
            skLineSegment(sketch, "E131", {"start": v(25.5, 76.42) * mm, "end": v(24.72, 75.73) * mm});
            skLineSegment(sketch, "E132", {"start": v(24.72, 75.73) * mm, "end": v(24.21, 75.1) * mm});
            skLineSegment(sketch, "E133", {"start": v(24.21, 75.1) * mm, "end": v(23.81, 74.24) * mm});
            skLineSegment(sketch, "E134", {"start": v(23.81, 74.24) * mm, "end": v(23.7, 73.31) * mm});
            skLineSegment(sketch, "E135", {"start": v(23.7, 73.31) * mm, "end": v(23.84, 72.73) * mm});
            skLineSegment(sketch, "E136", {"start": v(23.84, 72.73) * mm, "end": v(24.19, 71.9) * mm});
            skLineSegment(sketch, "E137", {"start": v(24.19, 71.9) * mm, "end": v(24.7, 71.32) * mm});
            skLineSegment(sketch, "E138", {"start": v(24.7, 71.32) * mm, "end": v(25.5, 71.02) * mm});
            skLineSegment(sketch, "E139", {"start": v(25.5, 71.02) * mm, "end": v(26.17, 71.02) * mm});
            skLineSegment(sketch, "E140", {"start": v(26.17, 71.02) * mm, "end": v(26.88, 71.27) * mm});
            skLineSegment(sketch, "E141", {"start": v(26.88, 71.27) * mm, "end": v(27.61, 72.02) * mm});
            skLineSegment(sketch, "E142", {"start": v(27.61, 72.02) * mm, "end": v(28.17, 73.3) * mm});
            skLineSegment(sketch, "E143", {"start": v(28.17, 73.3) * mm, "end": v(28.17, 74.42) * mm});
            skLineSegment(sketch, "E144", {"start": v(28.17, 74.42) * mm, "end": v(27.8, 75.99) * mm});
            skLineSegment(sketch, "E145", {"start": v(27.8, 75.99) * mm, "end": v(27.4, 76.93) * mm});
            skLineSegment(sketch, "E146", {"start": v(27.4, 76.93) * mm, "end": v(27.1, 77.4) * mm});
            skLineSegment(sketch, "E147", {"start": v(27.1, 77.4) * mm, "end": v(26.75, 77.98) * mm});
            skArc(sketch, "E148", {"start": v(22.86, 65.45) * mm, "mid": v(29.42, 70.28) * mm, "end": v(26.75, 77.98) * mm});
            skLineSegment(sketch, "E149.MirrorCS", {"start": v(19.55, 71.02) * mm, "end": v(18.84, 71.27) * mm});
            skLineSegment(sketch, "E150.MirrorCS", {"start": v(22.01, 73.31) * mm, "end": v(21.88, 72.73) * mm});
            skLineSegment(sketch, "E151.MirrorCS", {"start": v(18.61, 77.4) * mm, "end": v(18.97, 77.98) * mm});
            skLineSegment(sketch, "E152.MirrorCS", {"start": v(17.92, 75.99) * mm, "end": v(18.32, 76.93) * mm});
            skLineSegment(sketch, "E153.MirrorCS", {"start": v(21.53, 71.9) * mm, "end": v(21.02, 71.32) * mm});
            skLineSegment(sketch, "E154.MirrorCS", {"start": v(20.22, 71.02) * mm, "end": v(19.55, 71.02) * mm});
            skLineSegment(sketch, "E155.MirrorCS", {"start": v(21, 75.73) * mm, "end": v(21.5, 75.1) * mm});
            skLineSegment(sketch, "E156.MirrorCS", {"start": v(22.19, 75.98) * mm, "end": v(22.1, 76.79) * mm});
            skLineSegment(sketch, "E157.MirrorCS", {"start": v(20.9, 77.3) * mm, "end": v(21.7, 76.6) * mm});
            skLineSegment(sketch, "E158.MirrorCS", {"start": v(21.9, 74.24) * mm, "end": v(22.01, 73.31) * mm});
            skLineSegment(sketch, "E159.MirrorCS", {"start": v(18.32, 76.93) * mm, "end": v(18.61, 77.4) * mm});
            skLineSegment(sketch, "E160.MirrorCS", {"start": v(21.7, 76.6) * mm, "end": v(22.19, 75.98) * mm});
            skLineSegment(sketch, "E161.MirrorCS", {"start": v(21.88, 72.73) * mm, "end": v(21.53, 71.9) * mm});
            skLineSegment(sketch, "E162.MirrorCS", {"start": v(21.77, 77.61) * mm, "end": v(21.52, 78) * mm});
            skLineSegment(sketch, "E163.MirrorCS", {"start": v(21.5, 75.1) * mm, "end": v(21.9, 74.24) * mm});
            skLineSegment(sketch, "E164.MirrorCS", {"start": v(22.1, 76.79) * mm, "end": v(21.77, 77.61) * mm});
            skLineSegment(sketch, "E165.MirrorCS", {"start": v(21.02, 71.32) * mm, "end": v(20.22, 71.02) * mm});
            skLineSegment(sketch, "E166.MirrorCS", {"start": v(18.84, 71.27) * mm, "end": v(18.1, 72.02) * mm});
            skLineSegment(sketch, "E167.MirrorCS", {"start": v(20.9, 77.3) * mm, "end": v(20.22, 76.42) * mm});
            skLineSegment(sketch, "E168.MirrorCS", {"start": v(21.52, 78) * mm, "end": v(22.86, 79.54) * mm});
            skArc(sketch, "E169.MirrorCS", {"start": v(22.86, 65.45) * mm, "mid": v(16.3, 70.28) * mm, "end": v(18.97, 77.98) * mm});
            skLineSegment(sketch, "E170.MirrorCS", {"start": v(20.22, 76.42) * mm, "end": v(21, 75.73) * mm});
            skLineSegment(sketch, "E171.MirrorCS", {"start": v(17.55, 73.3) * mm, "end": v(17.55, 74.42) * mm});
            skLineSegment(sketch, "E172.MirrorCS", {"start": v(18.1, 72.02) * mm, "end": v(17.55, 73.3) * mm});
            skLineSegment(sketch, "E173.MirrorCS", {"start": v(17.55, 74.42) * mm, "end": v(17.92, 75.99) * mm});
            skCircle(sketch, "E174", {"center": v(-19.68, 32.38) * mm, "radius": 6.35 * mm});
            skLineSegment(sketch, "E175", {"start": v(-18.6, 36.94) * mm, "end": v(-19.68, 38.2) * mm});
            skLineSegment(sketch, "E176", {"start": v(-18.1, 36.39) * mm, "end": v(-17.54, 35.68) * mm});
            skLineSegment(sketch, "E177", {"start": v(-17.54, 35.68) * mm, "end": v(-17.84, 35.45) * mm});
            skLineSegment(sketch, "E178", {"start": v(-17.84, 35.45) * mm, "end": v(-18.3, 35) * mm});
            skLineSegment(sketch, "E179", {"start": v(-18.3, 35) * mm, "end": v(-18.6, 34.59) * mm});
            skLineSegment(sketch, "E180", {"start": v(-18.6, 34.59) * mm, "end": v(-18.91, 33.9) * mm});
            skLineSegment(sketch, "E181", {"start": v(-18.91, 33.9) * mm, "end": v(-19, 33.14) * mm});
            skLineSegment(sketch, "E182", {"start": v(-19, 33.14) * mm, "end": v(-18.92, 32.77) * mm});
            skLineSegment(sketch, "E183", {"start": v(-18.92, 32.77) * mm, "end": v(-18.62, 32.08) * mm});
            skLineSegment(sketch, "E184", {"start": v(-18.62, 32.08) * mm, "end": v(-18.41, 31.76) * mm});
            skLineSegment(sketch, "E185", {"start": v(-18.41, 31.76) * mm, "end": v(-17.99, 31.47) * mm});
            skLineSegment(sketch, "E186", {"start": v(-17.99, 31.47) * mm, "end": v(-17.5, 31.32) * mm});
            skLineSegment(sketch, "E187", {"start": v(-17.5, 31.32) * mm, "end": v(-17.12, 31.32) * mm});
            skLineSegment(sketch, "E188", {"start": v(-17.12, 31.32) * mm, "end": v(-16.5, 31.5) * mm});
            skLineSegment(sketch, "E189", {"start": v(-16.5, 31.5) * mm, "end": v(-15.86, 32.13) * mm});
            skLineSegment(sketch, "E190", {"start": v(-15.86, 32.13) * mm, "end": v(-15.4, 33.16) * mm});
            skLineSegment(sketch, "E191", {"start": v(-15.4, 33.16) * mm, "end": v(-15.4, 34.04) * mm});
            skLineSegment(sketch, "E192", {"start": v(-15.4, 34.04) * mm, "end": v(-15.7, 35.29) * mm});
            skLineSegment(sketch, "E193", {"start": v(-15.7, 35.29) * mm, "end": v(-16, 36) * mm});
            skLineSegment(sketch, "E194", {"start": v(-16, 36) * mm, "end": v(-16.29, 36.55) * mm});
            skLineSegment(sketch, "E195", {"start": v(-16.29, 36.55) * mm, "end": v(-16.58, 36.96) * mm});
            skLineSegment(sketch, "E196", {"start": v(-18.1, 36.39) * mm, "end": v(-18.3, 36.23) * mm});
            skLineSegment(sketch, "E197", {"start": v(-18.3, 36.23) * mm, "end": v(-18.67, 35.87) * mm});
            skLineSegment(sketch, "E198", {"start": v(-18.67, 35.87) * mm, "end": v(-18.94, 35.6) * mm});
            skLineSegment(sketch, "E199", {"start": v(-18.94, 35.6) * mm, "end": v(-19.16, 35.3) * mm});
            skLineSegment(sketch, "E200", {"start": v(-19.16, 35.3) * mm, "end": v(-19.06, 35.92) * mm});
            skLineSegment(sketch, "E201", {"start": v(-19.06, 35.92) * mm, "end": v(-18.9, 36.39) * mm});
            skLineSegment(sketch, "E202", {"start": v(-18.9, 36.39) * mm, "end": v(-18.76, 36.73) * mm});
            skLineSegment(sketch, "E203", {"start": v(-18.76, 36.73) * mm, "end": v(-18.6, 36.94) * mm});
            skPoint(sketch, "E204.start.orphan", {"position": v(-19.68, 38.73) * mm});
            skLineSegment(sketch, "E205.MirrorCS", {"start": v(-20.96, 31.76) * mm, "end": v(-21.38, 31.47) * mm});
            skLineSegment(sketch, "E206.MirrorCS", {"start": v(-23.37, 36) * mm, "end": v(-23.08, 36.55) * mm});
            skLineSegment(sketch, "E207.MirrorCS", {"start": v(-20.75, 32.08) * mm, "end": v(-20.96, 31.76) * mm});
            skLineSegment(sketch, "E208.MirrorCS", {"start": v(-23.96, 33.16) * mm, "end": v(-23.96, 34.04) * mm});
            skLineSegment(sketch, "E209.MirrorCS", {"start": v(-20.21, 35.3) * mm, "end": v(-20.3, 35.92) * mm});
            skLineSegment(sketch, "E210.MirrorCS", {"start": v(-21.53, 35.45) * mm, "end": v(-21.08, 35) * mm});
            skLineSegment(sketch, "E211.MirrorCS", {"start": v(-20.3, 35.92) * mm, "end": v(-20.47, 36.39) * mm});
            skLineSegment(sketch, "E212.MirrorCS", {"start": v(-20.47, 36.39) * mm, "end": v(-20.61, 36.73) * mm});
            skLineSegment(sketch, "E213.MirrorCS", {"start": v(-20.43, 35.6) * mm, "end": v(-20.21, 35.3) * mm});
            skLineSegment(sketch, "E214.MirrorCS", {"start": v(-22.25, 31.32) * mm, "end": v(-22.86, 31.5) * mm});
            skLineSegment(sketch, "E215.MirrorCS", {"start": v(-22.86, 31.5) * mm, "end": v(-23.51, 32.13) * mm});
            skLineSegment(sketch, "E216.MirrorCS", {"start": v(-23.08, 36.55) * mm, "end": v(-22.8, 36.96) * mm});
            skLineSegment(sketch, "E217.MirrorCS", {"start": v(-23.67, 35.29) * mm, "end": v(-23.37, 36) * mm});
            skLineSegment(sketch, "E218.MirrorCS", {"start": v(-21.07, 36.23) * mm, "end": v(-20.7, 35.87) * mm});
            skLineSegment(sketch, "E219.MirrorCS", {"start": v(-21.08, 35) * mm, "end": v(-20.76, 34.59) * mm});
            skLineSegment(sketch, "E220.MirrorCS", {"start": v(-21.38, 31.47) * mm, "end": v(-21.87, 31.32) * mm});
            skLineSegment(sketch, "E221.MirrorCS", {"start": v(-21.83, 35.68) * mm, "end": v(-21.53, 35.45) * mm});
            skLineSegment(sketch, "E222.MirrorCS", {"start": v(-21.28, 36.39) * mm, "end": v(-21.07, 36.23) * mm});
            skLineSegment(sketch, "E223.MirrorCS", {"start": v(-20.45, 32.77) * mm, "end": v(-20.75, 32.08) * mm});
            skLineSegment(sketch, "E224.MirrorCS", {"start": v(-21.28, 36.39) * mm, "end": v(-21.83, 35.68) * mm});
            skLineSegment(sketch, "E225.MirrorCS", {"start": v(-20.38, 33.14) * mm, "end": v(-20.45, 32.77) * mm});
            skLineSegment(sketch, "E226.MirrorCS", {"start": v(-20.76, 34.59) * mm, "end": v(-20.46, 33.9) * mm});
            skLineSegment(sketch, "E227.MirrorCS", {"start": v(-20.46, 33.9) * mm, "end": v(-20.38, 33.14) * mm});
            skLineSegment(sketch, "E228.MirrorCS", {"start": v(-20.7, 35.87) * mm, "end": v(-20.43, 35.6) * mm});
            skLineSegment(sketch, "E229.MirrorCS", {"start": v(-20.61, 36.73) * mm, "end": v(-20.78, 36.94) * mm});
            skLineSegment(sketch, "E230.MirrorCS", {"start": v(-21.87, 31.32) * mm, "end": v(-22.25, 31.32) * mm});
            skLineSegment(sketch, "E231.MirrorCS", {"start": v(-23.96, 34.04) * mm, "end": v(-23.67, 35.29) * mm});
            skLineSegment(sketch, "E232.MirrorCS", {"start": v(-20.78, 36.94) * mm, "end": v(-19.68, 38.2) * mm});
            skLineSegment(sketch, "E233.MirrorCS", {"start": v(-23.51, 32.13) * mm, "end": v(-23.96, 33.16) * mm});
            skArc(sketch, "E234", {"start": v(-22.8, 36.96) * mm, "mid": v(-19.68, 26.85) * mm, "end": v(-16.58, 36.96) * mm});
            skSolve(sketch);
        }
        {
            var Q0;
            Q0=makeQuery(id+"F29.imprint","IMPRINT",FACE,{"disambiguationData":[TD([[makeQuery(id+"F29.imprint","IMPRINT",EDGE,{"derivedFrom":sQuery(id+"F29.wireOp",EDGE,"E175")}),-1.0]])]});
            extrude(context, id + "F30", {"entities" : qUnion([Q0]), "operationType" : NewBodyOperationType.REMOVE, "oppositeDirection" : true, "depth" : 1.27 * mm, "offsetDistance" : 25.4 * mm});
        }
        {
            var Q0;
            {var subQ10=sQuery(id+"F1.wireOp",EDGE,"E1.top");var subQ18=sQuery(id+"F1.wireOp",EDGE,"E1.left");var subQ20=sQuery(id+"F15.wireOp",EDGE,"E34");var subQ21=sQuery(id+"F15.wireOp",EDGE,"E30.top");var subQ22=sQuery(id+"F15.wireOp",EDGE,"E31.top");var subQ24=sQuery(id+"F15.wireOp",EDGE,"E32.bottom");var subQ25=sQuery(id+"F15.wireOp",EDGE,"E37");Q0=makeQuery(id+"F30.boolean.opBoolean","SPLIT",FACE,{"disambiguationData":[TD([makeQuery(id+"F3.opShell","OFFSET_FACE",FACE,{"disambiguationData":[OSD([subQ18])]})])],"derivedFrom":makeQuery(id+"F22.boolean.opBoolean","MERGE",FACE,{"derivedFrom":[makeQuery(id+"F16.boolean.opBoolean","MERGE",FACE,{"derivedFrom":[makeQuery(id+"F2.opExtrude","SWEPT_FACE",FACE,{"disambiguationData":[OSD([subQ10])]}),makeQuery(id+"F16.opExtrude","CAP_FACE",FACE,{"disambiguationData":[OSD([subQ21,subQ22,sQuery(id+"F15.wireOp",EDGE,"E32.left"),subQ20])],"isStart":true}),makeQuery(id+"F16.opExtrude","CAP_FACE",FACE,{"disambiguationData":[OSD([subQ24,subQ20,sQuery(id+"F15.wireOp",EDGE,"E35.0"),subQ25])],"isStart":true})]}),makeQuery(id+"F22.opExtrude","CAP_FACE",FACE,{"disambiguationData":[OSD([sQuery(id+"F21.wireOp",EDGE,"E86.bottom"),sQuery(id+"F21.wireOp",EDGE,"E86.top"),sQuery(id+"F21.wireOp",EDGE,"E86.left"),sQuery(id+"F21.wireOp",EDGE,"E86.right")])],"isStart":true})]})});}
            var sketch = newSketch(context, id + "F31", { "sketchPlane" : qUnion([Q0])});
            skText(sketch, "E235", { "text": "T-70", "fontName": "OpenSans-Bold.ttf"});
            skText(sketch, "E236", { "text": "X-Wing", "fontName": "OpenSans-Bold.ttf"});
            skLineSegment(sketch, "E237", {"start": v(-2.4, 25.52) * mm, "end": v(-2.4, 27.43) * mm});
            const initialGuessF31  = {"E235": [-0.0107, 0.02743, 1, 0, 0.00576], "E236": [-0.02056, 0.01813, 1, 0, 0.0074]};
            skSetInitialGuess(sketch, initialGuessF31);
            skSolve(sketch);
        }
        {
            var Q0;
            Q0=qSketchRegion(id+"F31",true);
            extrude(context, id + "F32", {"entities" : qUnion([Q0]), "operationType" : NewBodyOperationType.REMOVE, "oppositeDirection" : true, "depth" : 0.76 * mm, "offsetDistance" : 25.4 * mm});
        }
        {
            var Q0;
            {var subQ0=sQuery(id+"F17.wireOp",EDGE,"E43");Q0=makeQuery(id+"F19.boolean.opBoolean","MERGE",FACE,{"derivedFrom":[makeQuery(id+"F18.opExtrude","SWEPT_FACE",FACE,{"disambiguationData":[OSD([subQ0])]}),makeQuery(id+"F19.opExtrude","SWEPT_FACE",FACE,{"disambiguationData":[OSD([subQ0])]})]});}
            var Q1;
            Q1=makeQuery(id+"F18.opExtrude","SWEPT_FACE",FACE,{"disambiguationData":[OSD([sQuery(id+"F17.wireOp",EDGE,"E47")])]});
            var Q2;
            {var subQ0=sQuery(id+"F17.wireOp",EDGE,"E51");Q2=makeQuery(id+"F19.boolean.opBoolean","MERGE",FACE,{"derivedFrom":[makeQuery(id+"F18.opExtrude","SWEPT_FACE",FACE,{"disambiguationData":[OSD([subQ0])]}),makeQuery(id+"F19.opExtrude","SWEPT_FACE",FACE,{"disambiguationData":[OSD([subQ0])]})]});}
            var Q3;
            {var subQ0=sQuery(id+"F17.wireOp",EDGE,"E65.MirrorCS");Q3=makeQuery(id+"F19.boolean.opBoolean","MERGE",FACE,{"derivedFrom":[makeQuery(id+"F18.opExtrude","SWEPT_FACE",FACE,{"disambiguationData":[OSD([subQ0])]}),makeQuery(id+"F19.opExtrude","SWEPT_FACE",FACE,{"disambiguationData":[OSD([subQ0])]})]});}
            var Q4;
            Q4=makeQuery(id+"F18.opExtrude","SWEPT_FACE",FACE,{"disambiguationData":[OSD([sQuery(id+"F17.wireOp",EDGE,"E62.MirrorCS")])]});
            var Q5;
            {var subQ0=sQuery(id+"F17.wireOp",EDGE,"E66.MirrorCS");Q5=makeQuery(id+"F19.boolean.opBoolean","MERGE",FACE,{"derivedFrom":[makeQuery(id+"F18.opExtrude","SWEPT_FACE",FACE,{"disambiguationData":[OSD([subQ0])]}),makeQuery(id+"F19.opExtrude","SWEPT_FACE",FACE,{"disambiguationData":[OSD([subQ0])]})]});}
            var Q6;
            {var subQ0=sQuery(id+"F17.wireOp",EDGE,"E44");Q6=makeQuery(id+"F22.boolean.opBoolean","INTERSECT",EDGE,{"derivedFrom":[makeQuery(id+"F19.boolean.opBoolean","MERGE",FACE,{"derivedFrom":[makeQuery(id+"F18.opExtrude","SWEPT_FACE",FACE,{"disambiguationData":[OSD([subQ0])]}),makeQuery(id+"F19.opExtrude","SWEPT_FACE",FACE,{"disambiguationData":[OSD([subQ0])]})]}),makeQuery(id+"F22.opExtrude","CAP_FACE",FACE,{"disambiguationData":[OSD([sQuery(id+"F21.wireOp",EDGE,"E86.bottom"),sQuery(id+"F21.wireOp",EDGE,"E86.top"),sQuery(id+"F21.wireOp",EDGE,"E86.left"),sQuery(id+"F21.wireOp",EDGE,"E86.right")])],"isStart":true})]});}
            var Q7;
            {var subQ0=sQuery(id+"F17.wireOp",EDGE,"E42");Q7=makeQuery(id+"F22.boolean.opBoolean","INTERSECT",EDGE,{"derivedFrom":[makeQuery(id+"F19.boolean.opBoolean","MERGE",FACE,{"derivedFrom":[makeQuery(id+"F18.opExtrude","SWEPT_FACE",FACE,{"disambiguationData":[OSD([subQ0])]}),makeQuery(id+"F19.opExtrude","SWEPT_FACE",FACE,{"disambiguationData":[OSD([subQ0])]})]}),makeQuery(id+"F22.opExtrude","CAP_FACE",FACE,{"disambiguationData":[OSD([sQuery(id+"F21.wireOp",EDGE,"E86.bottom"),sQuery(id+"F21.wireOp",EDGE,"E86.top"),sQuery(id+"F21.wireOp",EDGE,"E86.left"),sQuery(id+"F21.wireOp",EDGE,"E86.right")])],"isStart":true})]});}
            var Q8;
            Q8=makeQuery(id+"F22.boolean.opBoolean","INTERSECT",EDGE,{"derivedFrom":[makeQuery(id+"F18.opExtrude","SWEPT_FACE",FACE,{"disambiguationData":[OSD([sQuery(id+"F17.wireOp",EDGE,"E46")])]}),makeQuery(id+"F22.opExtrude","CAP_FACE",FACE,{"disambiguationData":[OSD([sQuery(id+"F21.wireOp",EDGE,"E86.bottom"),sQuery(id+"F21.wireOp",EDGE,"E86.top"),sQuery(id+"F21.wireOp",EDGE,"E86.left"),sQuery(id+"F21.wireOp",EDGE,"E86.right")])],"isStart":true})]});
            var Q9;
            Q9=makeQuery(id+"F22.boolean.opBoolean","INTERSECT",EDGE,{"derivedFrom":[makeQuery(id+"F18.opExtrude","SWEPT_FACE",FACE,{"disambiguationData":[OSD([sQuery(id+"F17.wireOp",EDGE,"E50")])]}),makeQuery(id+"F22.opExtrude","CAP_FACE",FACE,{"disambiguationData":[OSD([sQuery(id+"F21.wireOp",EDGE,"E86.bottom"),sQuery(id+"F21.wireOp",EDGE,"E86.top"),sQuery(id+"F21.wireOp",EDGE,"E86.left"),sQuery(id+"F21.wireOp",EDGE,"E86.right")])],"isStart":true})]});
            var Q10;
            Q10=makeQuery(id+"F22.boolean.opBoolean","INTERSECT",EDGE,{"derivedFrom":[makeQuery(id+"F18.opExtrude","SWEPT_FACE",FACE,{"disambiguationData":[OSD([sQuery(id+"F17.wireOp",EDGE,"E76.MirrorCS")])]}),makeQuery(id+"F22.opExtrude","CAP_FACE",FACE,{"disambiguationData":[OSD([sQuery(id+"F21.wireOp",EDGE,"E86.bottom"),sQuery(id+"F21.wireOp",EDGE,"E86.top"),sQuery(id+"F21.wireOp",EDGE,"E86.left"),sQuery(id+"F21.wireOp",EDGE,"E86.right")])],"isStart":true})]});
            var Q11;
            Q11=makeQuery(id+"F22.boolean.opBoolean","INTERSECT",EDGE,{"derivedFrom":[makeQuery(id+"F18.opExtrude","SWEPT_FACE",FACE,{"disambiguationData":[OSD([sQuery(id+"F17.wireOp",EDGE,"E79.MirrorCS")])]}),makeQuery(id+"F22.opExtrude","CAP_FACE",FACE,{"disambiguationData":[OSD([sQuery(id+"F21.wireOp",EDGE,"E86.bottom"),sQuery(id+"F21.wireOp",EDGE,"E86.top"),sQuery(id+"F21.wireOp",EDGE,"E86.left"),sQuery(id+"F21.wireOp",EDGE,"E86.right")])],"isStart":true})]});
            var Q12;
            {var subQ0=sQuery(id+"F17.wireOp",EDGE,"E69.MirrorCS");Q12=makeQuery(id+"F22.boolean.opBoolean","INTERSECT",EDGE,{"derivedFrom":[makeQuery(id+"F19.boolean.opBoolean","MERGE",FACE,{"derivedFrom":[makeQuery(id+"F18.opExtrude","SWEPT_FACE",FACE,{"disambiguationData":[OSD([subQ0])]}),makeQuery(id+"F19.opExtrude","SWEPT_FACE",FACE,{"disambiguationData":[OSD([subQ0])]})]}),makeQuery(id+"F22.opExtrude","CAP_FACE",FACE,{"disambiguationData":[OSD([sQuery(id+"F21.wireOp",EDGE,"E86.bottom"),sQuery(id+"F21.wireOp",EDGE,"E86.top"),sQuery(id+"F21.wireOp",EDGE,"E86.left"),sQuery(id+"F21.wireOp",EDGE,"E86.right")])],"isStart":true})]});}
            var Q13;
            Q13=makeQuery(id+"F22.boolean.opBoolean","INTERSECT",EDGE,{"derivedFrom":[makeQuery(id+"F18.opExtrude","SWEPT_FACE",FACE,{"disambiguationData":[OSD([sQuery(id+"F17.wireOp",EDGE,"E73.MirrorCS")])]}),makeQuery(id+"F22.opExtrude","CAP_FACE",FACE,{"disambiguationData":[OSD([sQuery(id+"F21.wireOp",EDGE,"E86.bottom"),sQuery(id+"F21.wireOp",EDGE,"E86.top"),sQuery(id+"F21.wireOp",EDGE,"E86.left"),sQuery(id+"F21.wireOp",EDGE,"E86.right")])],"isStart":true})]});
            var Q14;
            {var subQ0=sQuery(id+"F15.wireOp",EDGE,"E37");var subQ1=sQuery(id+"F15.wireOp",EDGE,"E34");var subQ2=makeQuery(id+"F16.opExtrude","CAP_FACE",FACE,{"disambiguationData":[OSD([sQuery(id+"F15.wireOp",EDGE,"E32.bottom"),subQ1,sQuery(id+"F15.wireOp",EDGE,"E35.0"),subQ0])],"isStart":true});var subQ5=sQuery(id+"F1.wireOp",EDGE,"E1.right");var subQ6=makeQuery(id+"F3.opShell","OFFSET_FACE",FACE,{"disambiguationData":[OSD([subQ5])]});var subQ7=makeQuery(id+"F16.opExtrude","CAP_FACE",FACE,{"disambiguationData":[OSD([sQuery(id+"F15.wireOp",EDGE,"E30.top"),sQuery(id+"F15.wireOp",EDGE,"E31.top"),sQuery(id+"F15.wireOp",EDGE,"E32.left"),subQ1])],"isStart":true});var subQ8=sQuery(id+"F1.wireOp",EDGE,"E1.top");var subQ9=makeQuery(id+"F2.opExtrude","SWEPT_FACE",FACE,{"disambiguationData":[OSD([subQ8])]});Q14=makeQuery(id+"F18.boolean.opBoolean","SPLIT",EDGE,{"disambiguationData":[topologyDisambiguationEdgeConnected([subQ9,subQ6,subQ7,subQ2]),TD([makeQuery(id+"F16.opExtrude","SWEPT_FACE",FACE,{"disambiguationData":[OSD([subQ0])]})])],"derivedFrom":makeQuery(id+"F3.opShell","OFFSET_EDGE",EDGE,{"disambiguationData":[OSD([subQ8,subQ5])]})});}
            var Q15;
            {var subQ0=sQuery(id+"F15.wireOp",EDGE,"E34");var subQ1=makeQuery(id+"F16.opExtrude","CAP_FACE",FACE,{"disambiguationData":[OSD([sQuery(id+"F15.wireOp",EDGE,"E32.bottom"),subQ0,sQuery(id+"F15.wireOp",EDGE,"E35.0"),sQuery(id+"F15.wireOp",EDGE,"E37")])],"isStart":true});var subQ3=sQuery(id+"F17.wireOp",EDGE,"E44");var subQ4=sQuery(id+"F1.wireOp",EDGE,"E1.right");var subQ5=makeQuery(id+"F3.opShell","OFFSET_FACE",FACE,{"disambiguationData":[OSD([subQ4])]});var subQ6=makeQuery(id+"F16.opExtrude","CAP_FACE",FACE,{"disambiguationData":[OSD([sQuery(id+"F15.wireOp",EDGE,"E30.top"),sQuery(id+"F15.wireOp",EDGE,"E31.top"),sQuery(id+"F15.wireOp",EDGE,"E32.left"),subQ0])],"isStart":true});var subQ7=sQuery(id+"F1.wireOp",EDGE,"E1.top");var subQ8=makeQuery(id+"F2.opExtrude","SWEPT_FACE",FACE,{"disambiguationData":[OSD([subQ7])]});Q15=makeQuery(id+"F18.boolean.opBoolean","SPLIT",EDGE,{"disambiguationData":[topologyDisambiguationEdgeConnected([subQ8,subQ5,subQ6,subQ1]),TD([makeQuery(id+"F18.opExtrude","SWEPT_FACE",FACE,{"disambiguationData":[OSD([subQ3])]})])],"derivedFrom":makeQuery(id+"F3.opShell","OFFSET_EDGE",EDGE,{"disambiguationData":[OSD([subQ7,subQ4])]})});}
            var Q16;
            {var subQ0=sQuery(id+"F15.wireOp",EDGE,"E34");var subQ1=makeQuery(id+"F16.opExtrude","CAP_FACE",FACE,{"disambiguationData":[OSD([sQuery(id+"F15.wireOp",EDGE,"E32.bottom"),subQ0,sQuery(id+"F15.wireOp",EDGE,"E35.0"),sQuery(id+"F15.wireOp",EDGE,"E37")])],"isStart":true});var subQ2=sQuery(id+"F1.wireOp",EDGE,"E1.right");var subQ3=makeQuery(id+"F3.opShell","OFFSET_FACE",FACE,{"disambiguationData":[OSD([subQ2])]});var subQ4=makeQuery(id+"F16.opExtrude","CAP_FACE",FACE,{"disambiguationData":[OSD([sQuery(id+"F15.wireOp",EDGE,"E30.top"),sQuery(id+"F15.wireOp",EDGE,"E31.top"),sQuery(id+"F15.wireOp",EDGE,"E32.left"),subQ0])],"isStart":true});var subQ5=sQuery(id+"F1.wireOp",EDGE,"E1.top");var subQ6=makeQuery(id+"F2.opExtrude","SWEPT_FACE",FACE,{"disambiguationData":[OSD([subQ5])]});var subQ7=sQuery(id+"F17.wireOp",EDGE,"E48");Q16=makeQuery(id+"F18.boolean.opBoolean","SPLIT",EDGE,{"disambiguationData":[topologyDisambiguationEdgeConnected([subQ6,subQ3,subQ4,subQ1]),TD([makeQuery(id+"F18.opExtrude","SWEPT_FACE",FACE,{"disambiguationData":[OSD([subQ7])]})])],"derivedFrom":makeQuery(id+"F3.opShell","OFFSET_EDGE",EDGE,{"disambiguationData":[OSD([subQ5,subQ2])]})});}
            var Q17;
            {var subQ0=sQuery(id+"F17.wireOp",EDGE,"E83.right");var subQ2=sQuery(id+"F17.wireOp",EDGE,"E73.MirrorCS");var subQ4=sQuery(id+"F15.wireOp",EDGE,"E31.top");Q17=makeQuery(id+"F22.boolean.opBoolean","INTERSECT",EDGE,{"derivedFrom":[makeQuery(id+"F18.boolean.opBoolean","SPLIT",FACE,{"disambiguationData":[TD([makeQuery(id+"F16.opExtrude","SWEPT_FACE",FACE,{"disambiguationData":[OSD([subQ4])]})])],"derivedFrom":makeQuery(id+"F18.opExtrude","SWEPT_FACE",FACE,{"disambiguationData":[OSD([subQ0]),TDD([makeQuery(id+"F17.imprint","IMPRINT",EDGE,{"disambiguationData":[TD([[makeQuery(id+"F17.imprint","INTERSECT",VERTEX,{"derivedFrom":[subQ2,subQ0]}),1.0]])],"derivedFrom":subQ0})])]})}),makeQuery(id+"F22.opExtrude","CAP_FACE",FACE,{"disambiguationData":[OSD([sQuery(id+"F21.wireOp",EDGE,"E86.bottom"),sQuery(id+"F21.wireOp",EDGE,"E86.top"),sQuery(id+"F21.wireOp",EDGE,"E86.left"),sQuery(id+"F21.wireOp",EDGE,"E86.right")])],"isStart":true})]});}
            var Q18;
            Q18=makeQuery(id+"F16.opExtrude","CAP_EDGE",EDGE,{"disambiguationData":[OSD([sQuery(id+"F15.wireOp",EDGE,"E31.top")])],"isStart":true});
            var Q19;
            Q19=makeQuery(id+"F16.opExtrude","CAP_EDGE",EDGE,{"disambiguationData":[OSD([sQuery(id+"F15.wireOp",EDGE,"E30.top")])],"isStart":true});
            var Q20;
            {var subQ0=sQuery(id+"F1.wireOp",EDGE,"E1.top");Q20=makeQuery(id+"F3.opShell","OFFSET_EDGE",EDGE,{"disambiguationData":[OSD([subQ0]),TDD([makeQuery(id+"F2.opExtrude","CAP_EDGE",EDGE,{"disambiguationData":[OSD([subQ0])],"isStart":true})])]});}
            var Q21;
            {var subQ0=sQuery(id+"F15.wireOp",EDGE,"E34");Q21=makeQuery(id+"F16.opExtrude","CAP_EDGE",EDGE,{"disambiguationData":[OSD([subQ0]),TDD([makeQuery(id+"F15.imprint","IMPRINT",EDGE,{"disambiguationData":[TD([[makeQuery(id+"F15.imprint","INTERSECT",VERTEX,{"derivedFrom":[sQuery(id+"F15.wireOp",EDGE,"E32.bottom"),subQ0]}),1.0]])],"derivedFrom":subQ0})])],"isStart":true});}
            var Q22;
            {var subQ0=sQuery(id+"F1.wireOp",EDGE,"E1.left");var subQ1=sQuery(id+"F15.wireOp",EDGE,"E30.top");var subQ3=sQuery(id+"F1.wireOp",EDGE,"E1.top");Q22=makeQuery(id+"F16.boolean.opBoolean","SPLIT",EDGE,{"disambiguationData":[TD([makeQuery(id+"F16.opExtrude","SWEPT_FACE",FACE,{"disambiguationData":[OSD([subQ1])]})])],"derivedFrom":makeQuery(id+"F3.opShell","OFFSET_EDGE",EDGE,{"disambiguationData":[OSD([subQ3,subQ0])]})});}
            var Q23;
            {var subQ0=sQuery(id+"F1.wireOp",EDGE,"E1.left");var subQ2=sQuery(id+"F15.wireOp",EDGE,"E31.top");var subQ4=sQuery(id+"F1.wireOp",EDGE,"E1.top");Q23=makeQuery(id+"F16.boolean.opBoolean","SPLIT",EDGE,{"disambiguationData":[TD([makeQuery(id+"F16.opExtrude","SWEPT_FACE",FACE,{"disambiguationData":[OSD([subQ2])]})])],"derivedFrom":makeQuery(id+"F3.opShell","OFFSET_EDGE",EDGE,{"disambiguationData":[OSD([subQ4,subQ0])]})});}
            var Q24;
            {var subQ0=sQuery(id+"F1.wireOp",EDGE,"E1.left");var subQ1=sQuery(id+"F15.wireOp",EDGE,"E34");var subQ2=makeQuery(id+"F16.opExtrude","CAP_FACE",FACE,{"disambiguationData":[OSD([sQuery(id+"F15.wireOp",EDGE,"E30.top"),sQuery(id+"F15.wireOp",EDGE,"E31.top"),sQuery(id+"F15.wireOp",EDGE,"E32.left"),subQ1])],"isStart":true});var subQ3=sQuery(id+"F1.wireOp",EDGE,"E1.right");var subQ4=sQuery(id+"F1.wireOp",EDGE,"E1.top");var subQ5=sQuery(id+"F1.wireOp",EDGE,"E1.bottom");var subQ6=makeQuery(id+"F3.opShell","OFFSET_FACE",FACE,{"disambiguationData":[OSD([subQ5,subQ4,subQ0,subQ3]),TDD([makeQuery(id+"F2.opExtrude","CAP_FACE",FACE,{"disambiguationData":[OSD([subQ5,subQ4,subQ0,subQ3])],"isStart":false})])]});var subQ7=makeQuery(id+"F2.opExtrude","SWEPT_FACE",FACE,{"disambiguationData":[OSD([subQ4])]});var subQ8=makeQuery(id+"F16.opExtrude","CAP_FACE",FACE,{"disambiguationData":[OSD([sQuery(id+"F15.wireOp",EDGE,"E32.bottom"),subQ1,sQuery(id+"F15.wireOp",EDGE,"E35.0"),sQuery(id+"F15.wireOp",EDGE,"E37")])],"isStart":true});Q24=makeQuery(id+"F18.boolean.opBoolean","SPLIT",EDGE,{"disambiguationData":[topologyDisambiguationEdgeConnected([subQ7,subQ6,subQ2,subQ8]),TD([makeQuery(id+"F3.opShell","OFFSET_FACE",FACE,{"disambiguationData":[OSD([subQ0])]})])],"derivedFrom":makeQuery(id+"F3.opShell","OFFSET_EDGE",EDGE,{"disambiguationData":[OSD([subQ4]),TDD([makeQuery(id+"F2.opExtrude","CAP_EDGE",EDGE,{"disambiguationData":[OSD([subQ4])],"isStart":false})])]})});}
            var Q25;
            Q25=makeQuery(id+"F22.boolean.opBoolean","INTERSECT",EDGE,{"derivedFrom":[makeQuery(id+"F18.opExtrude","SWEPT_FACE",FACE,{"disambiguationData":[OSD([sQuery(id+"F17.wireOp",EDGE,"E48")])]}),makeQuery(id+"F22.opExtrude","CAP_FACE",FACE,{"disambiguationData":[OSD([sQuery(id+"F21.wireOp",EDGE,"E86.bottom"),sQuery(id+"F21.wireOp",EDGE,"E86.top"),sQuery(id+"F21.wireOp",EDGE,"E86.left"),sQuery(id+"F21.wireOp",EDGE,"E86.right")])],"isStart":true})]});
            var Q26;
            {var subQ2=sQuery(id+"F15.wireOp",EDGE,"E34");var subQ3=sQuery(id+"F15.wireOp",EDGE,"E32.bottom");var subQ4=sQuery(id+"F17.wireOp",EDGE,"E69.MirrorCS");var subQ5=sQuery(id+"F17.wireOp",EDGE,"E83.right");var subQ6=sQuery(id+"F15.wireOp",EDGE,"E30.top");Q26=makeQuery(id+"F22.boolean.opBoolean","INTERSECT",EDGE,{"derivedFrom":[makeQuery(id+"F19.boolean.opBoolean","SPLIT",FACE,{"disambiguationData":[TD([makeQuery(id+"F16.opExtrude","SWEPT_FACE",FACE,{"disambiguationData":[OSD([subQ6])]})])],"derivedFrom":makeQuery(id+"F18.boolean.opBoolean","MERGE",FACE,{"derivedFrom":[makeQuery(id+"F16.opExtrude","SWEPT_FACE",FACE,{"disambiguationData":[OSD([subQ2]),TDD([makeQuery(id+"F15.imprint","IMPRINT",EDGE,{"disambiguationData":[TD([[makeQuery(id+"F15.imprint","INTERSECT",VERTEX,{"derivedFrom":[subQ3,subQ2]}),1.0]])],"derivedFrom":subQ2})])]}),makeQuery(id+"F18.opExtrude","SWEPT_FACE",FACE,{"disambiguationData":[OSD([subQ5]),TDD([makeQuery(id+"F17.imprint","IMPRINT",EDGE,{"disambiguationData":[TD([[makeQuery(id+"F17.imprint","INTERSECT",VERTEX,{"derivedFrom":[subQ4,subQ5]}),-1.0]])],"derivedFrom":subQ5})])]})]})}),makeQuery(id+"F22.opExtrude","CAP_FACE",FACE,{"disambiguationData":[OSD([sQuery(id+"F21.wireOp",EDGE,"E86.bottom"),sQuery(id+"F21.wireOp",EDGE,"E86.top"),sQuery(id+"F21.wireOp",EDGE,"E86.left"),sQuery(id+"F21.wireOp",EDGE,"E86.right")])],"isStart":true})]});}
            var Q27;
            Q27=makeQuery(id+"F16.opExtrude","CAP_EDGE",EDGE,{"disambiguationData":[OSD([sQuery(id+"F15.wireOp",EDGE,"E37")])],"isStart":true});
            var Q28;
            {var subQ0=sQuery(id+"F17.wireOp",EDGE,"E70.MirrorCS");Q28=makeQuery(id+"F22.boolean.opBoolean","INTERSECT",EDGE,{"derivedFrom":[makeQuery(id+"F19.boolean.opBoolean","MERGE",FACE,{"derivedFrom":[makeQuery(id+"F18.opExtrude","SWEPT_FACE",FACE,{"disambiguationData":[OSD([subQ0])]}),makeQuery(id+"F19.opExtrude","SWEPT_FACE",FACE,{"disambiguationData":[OSD([subQ0])]})]}),makeQuery(id+"F22.opExtrude","CAP_FACE",FACE,{"disambiguationData":[OSD([sQuery(id+"F21.wireOp",EDGE,"E86.bottom"),sQuery(id+"F21.wireOp",EDGE,"E86.top"),sQuery(id+"F21.wireOp",EDGE,"E86.left"),sQuery(id+"F21.wireOp",EDGE,"E86.right")])],"isStart":true})]});}
            var Q29;
            {var subQ0=sQuery(id+"F17.wireOp",EDGE,"E83.top");Q29=makeQuery(id+"F19.boolean.opBoolean","INTERSECT",EDGE,{"derivedFrom":[makeQuery(id+"F10.boolean.opBoolean","MERGE",FACE,{"derivedFrom":[makeQuery(id+"F2.opExtrude","CAP_FACE",FACE,{"disambiguationData":[OSD([sQuery(id+"F1.wireOp",EDGE,"E1.bottom"),sQuery(id+"F1.wireOp",EDGE,"E1.top"),sQuery(id+"F1.wireOp",EDGE,"E1.left"),sQuery(id+"F1.wireOp",EDGE,"E1.right")])],"isStart":false}),makeQuery(id+"F10.opExtrude","SWEPT_FACE",FACE,{"disambiguationData":[OSD([sQuery(id+"F9.wireOp",EDGE,"E10.bottom")])]}),makeQuery(id+"F10.opExtrude","SWEPT_FACE",FACE,{"disambiguationData":[OSD([sQuery(id+"F9.wireOp",EDGE,"E19.MirrorCS")])]})]}),makeQuery(id+"F19.opExtrude","SWEPT_FACE",FACE,{"disambiguationData":[OSD([subQ0]),TDD([makeQuery(id+"F17.imprint","IMPRINT",EDGE,{"disambiguationData":[TD([[makeQuery(id+"F17.imprint","INTERSECT",VERTEX,{"derivedFrom":[sQuery(id+"F17.wireOp",EDGE,"E55"),subQ0]}),1.0]])],"derivedFrom":subQ0})])]})]});}
            var Q30;
            {var subQ0=sQuery(id+"F17.wireOp",EDGE,"E83.top");Q30=makeQuery(id+"F19.boolean.opBoolean","INTERSECT",EDGE,{"derivedFrom":[makeQuery(id+"F10.boolean.opBoolean","MERGE",FACE,{"derivedFrom":[makeQuery(id+"F2.opExtrude","CAP_FACE",FACE,{"disambiguationData":[OSD([sQuery(id+"F1.wireOp",EDGE,"E1.bottom"),sQuery(id+"F1.wireOp",EDGE,"E1.top"),sQuery(id+"F1.wireOp",EDGE,"E1.left"),sQuery(id+"F1.wireOp",EDGE,"E1.right")])],"isStart":false}),makeQuery(id+"F10.opExtrude","SWEPT_FACE",FACE,{"disambiguationData":[OSD([sQuery(id+"F9.wireOp",EDGE,"E10.bottom")])]}),makeQuery(id+"F10.opExtrude","SWEPT_FACE",FACE,{"disambiguationData":[OSD([sQuery(id+"F9.wireOp",EDGE,"E19.MirrorCS")])]})]}),makeQuery(id+"F19.opExtrude","SWEPT_FACE",FACE,{"disambiguationData":[OSD([subQ0]),TDD([makeQuery(id+"F17.imprint","IMPRINT",EDGE,{"disambiguationData":[TD([[makeQuery(id+"F17.imprint","INTERSECT",VERTEX,{"derivedFrom":[sQuery(id+"F17.wireOp",EDGE,"E68.MirrorCS"),subQ0]}),-1.0]])],"derivedFrom":subQ0})])]})]});}
            var Q31;
            {var subQ0=sQuery(id+"F27.wireOp",EDGE,"E98");Q31=makeQuery(id+"F28.boolean.opBoolean","MERGE",EDGE,{"derivedFrom":[makeQuery(id+"F19.boolean.opBoolean","COPY",EDGE,{"derivedFrom":makeQuery(id+"F19.opExtrude","SWEPT_EDGE",EDGE,{"disambiguationData":[OSD([sQuery(id+"F17.wireOp",EDGE,"E55"),sQuery(id+"F17.wireOp",EDGE,"E83.top")])]})}),makeQuery(id+"F28.opExtrude","TWEAK_EDGE",EDGE,{"derivedFrom":[makeQuery(id+"F27.imprint","IMPRINT",EDGE,{"disambiguationData":[TD([[makeQuery(id+"F27.imprint","INTERSECT",VERTEX,{"derivedFrom":[sQuery(id+"F27.wireOp",EDGE,"E97.0"),subQ0]}),1.0]])],"derivedFrom":subQ0}),dummyQuery(id+"F28.vertexPlane.planeOp",FACE)]})]});}
            var Q32;
            {var subQ0=sQuery(id+"F25.wireOp",EDGE,"E94");Q32=makeQuery(id+"F26.boolean.opBoolean","MERGE",EDGE,{"derivedFrom":[makeQuery(id+"F19.boolean.opBoolean","COPY",EDGE,{"derivedFrom":makeQuery(id+"F19.opExtrude","SWEPT_EDGE",EDGE,{"disambiguationData":[OSD([sQuery(id+"F17.wireOp",EDGE,"E68.MirrorCS"),sQuery(id+"F17.wireOp",EDGE,"E83.top")])]})}),makeQuery(id+"F26.opExtrude","TWEAK_EDGE",EDGE,{"derivedFrom":[makeQuery(id+"F25.imprint","IMPRINT",EDGE,{"disambiguationData":[TD([[makeQuery(id+"F25.imprint","INTERSECT",VERTEX,{"derivedFrom":[sQuery(id+"F25.wireOp",EDGE,"E92.0"),subQ0]}),-1.0]])],"derivedFrom":subQ0}),dummyQuery(id+"F26.vertexPlane.planeOp",FACE)]})]});}
            var Q33;
            Q33=makeQuery(id+"F19.boolean.opBoolean","INTERSECT",EDGE,{"derivedFrom":[makeQuery(id+"F10.boolean.opBoolean","MERGE",FACE,{"derivedFrom":[makeQuery(id+"F2.opExtrude","CAP_FACE",FACE,{"disambiguationData":[OSD([sQuery(id+"F1.wireOp",EDGE,"E1.bottom"),sQuery(id+"F1.wireOp",EDGE,"E1.top"),sQuery(id+"F1.wireOp",EDGE,"E1.left"),sQuery(id+"F1.wireOp",EDGE,"E1.right")])],"isStart":false}),makeQuery(id+"F10.opExtrude","SWEPT_FACE",FACE,{"disambiguationData":[OSD([sQuery(id+"F9.wireOp",EDGE,"E10.bottom")])]}),makeQuery(id+"F10.opExtrude","SWEPT_FACE",FACE,{"disambiguationData":[OSD([sQuery(id+"F9.wireOp",EDGE,"E19.MirrorCS")])]})]}),makeQuery(id+"F19.opExtrude","SWEPT_FACE",FACE,{"disambiguationData":[OSD([sQuery(id+"F17.wireOp",EDGE,"E55")])]})]});
            var Q34;
            Q34=makeQuery(id+"F19.boolean.opBoolean","INTERSECT",EDGE,{"derivedFrom":[makeQuery(id+"F10.boolean.opBoolean","MERGE",FACE,{"derivedFrom":[makeQuery(id+"F2.opExtrude","CAP_FACE",FACE,{"disambiguationData":[OSD([sQuery(id+"F1.wireOp",EDGE,"E1.bottom"),sQuery(id+"F1.wireOp",EDGE,"E1.top"),sQuery(id+"F1.wireOp",EDGE,"E1.left"),sQuery(id+"F1.wireOp",EDGE,"E1.right")])],"isStart":false}),makeQuery(id+"F10.opExtrude","SWEPT_FACE",FACE,{"disambiguationData":[OSD([sQuery(id+"F9.wireOp",EDGE,"E10.bottom")])]}),makeQuery(id+"F10.opExtrude","SWEPT_FACE",FACE,{"disambiguationData":[OSD([sQuery(id+"F9.wireOp",EDGE,"E19.MirrorCS")])]})]}),makeQuery(id+"F19.opExtrude","SWEPT_FACE",FACE,{"disambiguationData":[OSD([sQuery(id+"F17.wireOp",EDGE,"E68.MirrorCS")])]})]});
            var Q35;
            Q35=makeQuery(id+"F19.boolean.opBoolean","INTERSECT",EDGE,{"derivedFrom":[makeQuery(id+"F10.boolean.opBoolean","MERGE",FACE,{"derivedFrom":[makeQuery(id+"F2.opExtrude","CAP_FACE",FACE,{"disambiguationData":[OSD([sQuery(id+"F1.wireOp",EDGE,"E1.bottom"),sQuery(id+"F1.wireOp",EDGE,"E1.top"),sQuery(id+"F1.wireOp",EDGE,"E1.left"),sQuery(id+"F1.wireOp",EDGE,"E1.right")])],"isStart":false}),makeQuery(id+"F10.opExtrude","SWEPT_FACE",FACE,{"disambiguationData":[OSD([sQuery(id+"F9.wireOp",EDGE,"E10.bottom")])]}),makeQuery(id+"F10.opExtrude","SWEPT_FACE",FACE,{"disambiguationData":[OSD([sQuery(id+"F9.wireOp",EDGE,"E19.MirrorCS")])]})]}),makeQuery(id+"F19.opExtrude","SWEPT_FACE",FACE,{"disambiguationData":[OSD([sQuery(id+"F17.wireOp",EDGE,"E56"),sQuery(id+"F17.wireOp",EDGE,"E63.MirrorCS")])]})]});
            var Q36;
            {var subQ0=sQuery(id+"F17.wireOp",EDGE,"E83.left");Q36=makeQuery(id+"F19.boolean.opBoolean","INTERSECT",EDGE,{"derivedFrom":[makeQuery(id+"F13.opFillet","BLEND_FACE",FACE,{"disambiguationData":[OSD([sQuery(id+"F1.wireOp",EDGE,"E1.right"),sQuery(id+"F9.wireOp",EDGE,"E18.MirrorCS"),sQuery(id+"F9.wireOp",EDGE,"E19.MirrorCS")])]}),makeQuery(id+"F19.opExtrude","SWEPT_FACE",FACE,{"disambiguationData":[OSD([subQ0]),TDD([makeQuery(id+"F17.imprint","IMPRINT",EDGE,{"disambiguationData":[TD([[makeQuery(id+"F17.imprint","INTERSECT",VERTEX,{"derivedFrom":[sQuery(id+"F17.wireOp",EDGE,"E52"),subQ0]}),-1.0]])],"derivedFrom":subQ0})])]})]});}
            var Q37;
            {var subQ0=sQuery(id+"F17.wireOp",EDGE,"E83.right");Q37=makeQuery(id+"F19.boolean.opBoolean","INTERSECT",EDGE,{"derivedFrom":[makeQuery(id+"F10.boolean.opBoolean","MERGE",FACE,{"derivedFrom":[makeQuery(id+"F2.opExtrude","CAP_FACE",FACE,{"disambiguationData":[OSD([sQuery(id+"F1.wireOp",EDGE,"E1.bottom"),sQuery(id+"F1.wireOp",EDGE,"E1.top"),sQuery(id+"F1.wireOp",EDGE,"E1.left"),sQuery(id+"F1.wireOp",EDGE,"E1.right")])],"isStart":false}),makeQuery(id+"F10.opExtrude","SWEPT_FACE",FACE,{"disambiguationData":[OSD([sQuery(id+"F9.wireOp",EDGE,"E10.bottom")])]}),makeQuery(id+"F10.opExtrude","SWEPT_FACE",FACE,{"disambiguationData":[OSD([sQuery(id+"F9.wireOp",EDGE,"E19.MirrorCS")])]})]}),makeQuery(id+"F19.opExtrude","SWEPT_FACE",FACE,{"disambiguationData":[OSD([subQ0]),TDD([makeQuery(id+"F17.imprint","IMPRINT",EDGE,{"disambiguationData":[TD([[makeQuery(id+"F17.imprint","INTERSECT",VERTEX,{"derivedFrom":[sQuery(id+"F17.wireOp",EDGE,"E74.MirrorCS"),subQ0]}),-1.0]])],"derivedFrom":subQ0})])]})]});}
            fillet(context, id + "F33", {"entities" : qUnion([Q0, Q1, Q2, Q3, Q4, Q5, Q6, Q7, Q8, Q9, Q10, Q11, Q12, Q13, Q14, Q15, Q16, Q17, Q18, Q19, Q20, Q21, Q22, Q23, Q24, Q25, Q26, Q27, Q28, Q29, Q30, Q31, Q32, Q33, Q34, Q35, Q36, Q37]), "radius" : 0.25 * mm, "tangentPropagation" : true, "allowEdgeOverflow" : false});
        }
        {
            var Q0;
            {var subQ2=sQuery(id+"F17.wireOp",EDGE,"E74.MirrorCS");var subQ5=sQuery(id+"F1.wireOp",EDGE,"E1.top");var subQ6=sQuery(id+"F17.wireOp",EDGE,"E83.right");Q0=makeQuery(id+"F22.boolean.opBoolean","INTERSECT",EDGE,{"derivedFrom":[makeQuery(id+"F18.boolean.opBoolean","SPLIT",FACE,{"disambiguationData":[TD([makeQuery(id+"F2.opExtrude","SWEPT_FACE",FACE,{"disambiguationData":[OSD([subQ5])]})])],"derivedFrom":makeQuery(id+"F18.opExtrude","SWEPT_FACE",FACE,{"disambiguationData":[OSD([subQ6]),TDD([makeQuery(id+"F17.imprint","IMPRINT",EDGE,{"disambiguationData":[TD([[makeQuery(id+"F17.imprint","INTERSECT",VERTEX,{"derivedFrom":[subQ2,subQ6]}),1.0]])],"derivedFrom":subQ6})])]})}),makeQuery(id+"F22.opExtrude","CAP_FACE",FACE,{"disambiguationData":[OSD([sQuery(id+"F21.wireOp",EDGE,"E86.bottom"),sQuery(id+"F21.wireOp",EDGE,"E86.top"),sQuery(id+"F21.wireOp",EDGE,"E86.left"),sQuery(id+"F21.wireOp",EDGE,"E86.right")])],"isStart":true})]});}
            var Q1;
            Q1=makeQuery(id+"F19.boolean.opBoolean","COPY",EDGE,{"derivedFrom":makeQuery(id+"F19.opExtrude","SWEPT_EDGE",EDGE,{"disambiguationData":[OSD([sQuery(id+"F17.wireOp",EDGE,"E83.bottom"),sQuery(id+"F17.wireOp",EDGE,"E83.right")])]})});
            var Q2;
            {var subQ0=sQuery(id+"F17.wireOp",EDGE,"E83.right");var subQ1=sQuery(id+"F17.wireOp",EDGE,"E69.MirrorCS");Q2=makeQuery(id+"F19.boolean.opBoolean","MERGE",EDGE,{"derivedFrom":[makeQuery(id+"F18.opExtrude","SWEPT_EDGE",EDGE,{"disambiguationData":[OSD([subQ1,subQ0])]}),makeQuery(id+"F19.opExtrude","SWEPT_EDGE",EDGE,{"disambiguationData":[OSD([subQ1,subQ0])]})]});}
            var Q3;
            {var subQ0=sQuery(id+"F17.wireOp",EDGE,"E73.MirrorCS");var subQ1=sQuery(id+"F17.wireOp",EDGE,"E83.right");Q3=makeQuery(id+"F18.boolean.opBoolean","SPLIT",EDGE,{"disambiguationData":[topologyDisambiguationEdgeConnected([makeQuery(id+"F18.opExtrude","SWEPT_FACE",FACE,{"disambiguationData":[OSD([subQ1]),TDD([makeQuery(id+"F17.imprint","IMPRINT",EDGE,{"disambiguationData":[TD([[makeQuery(id+"F17.imprint","INTERSECT",VERTEX,{"derivedFrom":[subQ0,subQ1]}),1.0]])],"derivedFrom":subQ1})])]})])],"derivedFrom":makeQuery(id+"F18.opExtrude","SWEPT_EDGE",EDGE,{"disambiguationData":[OSD([subQ0,subQ1])]})});}
            var Q4;
            {var subQ0=sQuery(id+"F17.wireOp",EDGE,"E79.MirrorCS");var subQ1=makeQuery(id+"F18.opExtrude","SWEPT_FACE",FACE,{"disambiguationData":[OSD([subQ0])]});var subQ2=sQuery(id+"F17.wireOp",EDGE,"E83.right");var subQ3=sQuery(id+"F17.wireOp",EDGE,"E73.MirrorCS");var subQ5=sQuery(id+"F15.wireOp",EDGE,"E31.top");var subQ6=makeQuery(id+"F18.opExtrude","SWEPT_FACE",FACE,{"disambiguationData":[OSD([subQ2]),TDD([makeQuery(id+"F17.imprint","IMPRINT",EDGE,{"disambiguationData":[TD([[makeQuery(id+"F17.imprint","INTERSECT",VERTEX,{"derivedFrom":[subQ3,subQ2]}),1.0]])],"derivedFrom":subQ2})])]});Q4=makeQuery(id+"F18.boolean.opBoolean","SPLIT",EDGE,{"disambiguationData":[topologyDisambiguationEdgeConnected([subQ1,subQ6]),TD([makeQuery(id+"F16.opExtrude","SWEPT_FACE",FACE,{"disambiguationData":[OSD([subQ5])]})])],"derivedFrom":makeQuery(id+"F18.opExtrude","SWEPT_EDGE",EDGE,{"disambiguationData":[OSD([subQ0,subQ2])]})});}
            fillet(context, id + "F34", {"entities" : qUnion([Q0, Q1, Q2, Q3, Q4]), "radius" : 0.25 * mm, "tangentPropagation" : true, "allowEdgeOverflow" : false});
        }
    });
